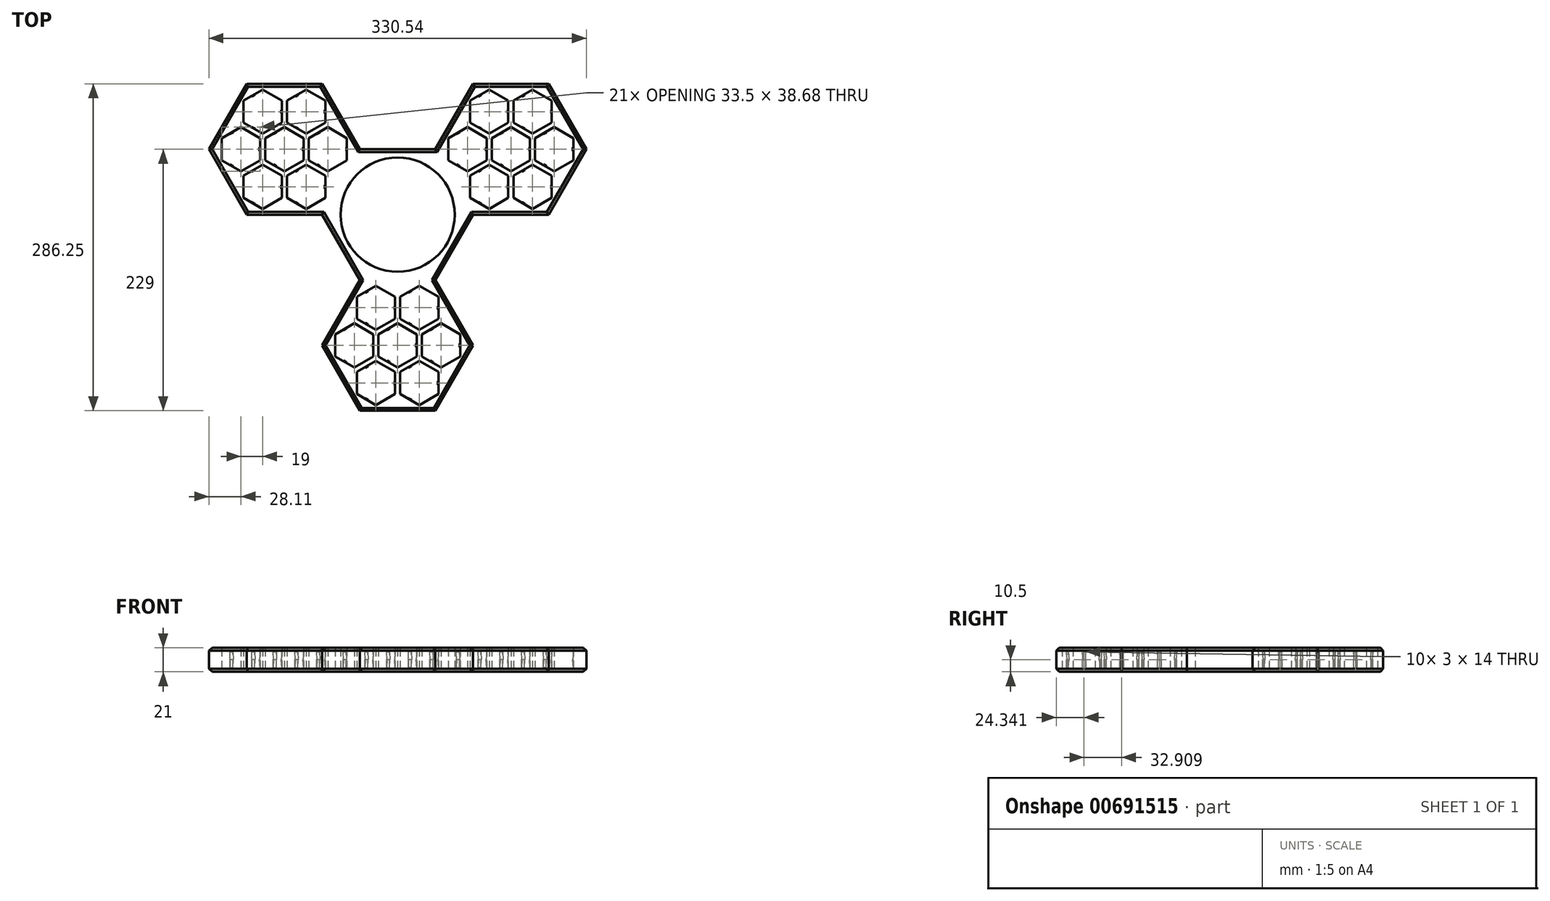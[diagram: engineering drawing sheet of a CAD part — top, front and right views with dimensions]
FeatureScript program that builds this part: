
annotation { "Feature Type Name" : "Feature", "Feature Type Description" : "" }
export const myFeature = defineFeature(function(context is Context, id is Id, definition is map)
    precondition{}
    {
        {
            var Q0;
            Q0=qCreatedBy(makeId("Top.planeOp"),FACE);
            var sketch = newSketch(context, id + "F0", { "sketchPlane" : qUnion([Q0])});
            skCircle(sketch, "E0", {"center": v(0, 0) * mm, "radius": 50 * mm});
            skCircle(sketch, "E1.cCircle", {"center": v(0, 0) * mm, "radius": 57.25 * mm, "construction": true});
            skLineSegment(sketch, "E1.0", {"start": v(-33.05, 57.25) * mm, "end": v(33.05, 57.25) * mm});
            skLineSegment(sketch, "E1.2", {"start": v(66.1, 0) * mm, "end": v(33.05, -57.25) * mm});
            skLineSegment(sketch, "E1.4", {"start": v(-33.05, -57.25) * mm, "end": v(-66.1, 0) * mm});
            skPoint(sketch, "E1.0.midPoint", {"position": v(0, 57.25) * mm});
            skCircle(sketch, "E2.cCircle", {"center": v(-61.16, 57.25) * mm, "radius": 16.75 * mm, "construction": true});
            skLineSegment(sketch, "E2.0", {"start": v(-44.4, 66.92) * mm, "end": v(-44.4, 47.58) * mm});
            skLineSegment(sketch, "E2.1", {"start": v(-44.4, 47.58) * mm, "end": v(-61.16, 37.9) * mm});
            skLineSegment(sketch, "E2.2", {"start": v(-61.16, 37.9) * mm, "end": v(-77.9, 47.58) * mm});
            skLineSegment(sketch, "E2.3", {"start": v(-77.9, 47.58) * mm, "end": v(-77.9, 66.92) * mm});
            skLineSegment(sketch, "E2.4", {"start": v(-77.9, 66.92) * mm, "end": v(-61.16, 76.6) * mm});
            skLineSegment(sketch, "E2.5", {"start": v(-61.16, 76.6) * mm, "end": v(-44.4, 66.92) * mm});
            skPoint(sketch, "E2.0.midPoint", {"position": v(-44.4, 57.25) * mm});
            skCircle(sketch, "E3.cCircle", {"center": v(-80.16, 24.34) * mm, "radius": 16.75 * mm, "construction": true});
            skLineSegment(sketch, "E3.0", {"start": v(-63.4, 34.01) * mm, "end": v(-63.4, 14.67) * mm});
            skLineSegment(sketch, "E3.1", {"start": v(-63.4, 14.67) * mm, "end": v(-80.16, 5) * mm});
            skLineSegment(sketch, "E3.2", {"start": v(-80.16, 5) * mm, "end": v(-96.9, 14.67) * mm});
            skLineSegment(sketch, "E3.3", {"start": v(-96.9, 14.67) * mm, "end": v(-96.9, 34.01) * mm});
            skLineSegment(sketch, "E3.4", {"start": v(-96.9, 34.01) * mm, "end": v(-80.16, 43.68) * mm});
            skLineSegment(sketch, "E3.5", {"start": v(-80.16, 43.68) * mm, "end": v(-63.4, 34.01) * mm});
            skPoint(sketch, "E3.0.midPoint", {"position": v(-63.4, 24.34) * mm});
            skCircle(sketch, "E4.cCircle", {"center": v(-99.16, 57.25) * mm, "radius": 16.75 * mm, "construction": true});
            skLineSegment(sketch, "E4.0", {"start": v(-82.4, 66.92) * mm, "end": v(-82.4, 47.58) * mm});
            skLineSegment(sketch, "E4.1", {"start": v(-82.4, 47.58) * mm, "end": v(-99.16, 37.9) * mm});
            skLineSegment(sketch, "E4.2", {"start": v(-99.16, 37.9) * mm, "end": v(-115.9, 47.58) * mm});
            skLineSegment(sketch, "E4.3", {"start": v(-115.9, 47.58) * mm, "end": v(-115.9, 66.92) * mm});
            skLineSegment(sketch, "E4.4", {"start": v(-115.9, 66.92) * mm, "end": v(-99.16, 76.6) * mm});
            skLineSegment(sketch, "E4.5", {"start": v(-99.16, 76.6) * mm, "end": v(-82.4, 66.92) * mm});
            skPoint(sketch, "E4.0.midPoint", {"position": v(-82.4, 57.25) * mm});
            skCircle(sketch, "E5.cCircle", {"center": v(-118.16, 24.34) * mm, "radius": 16.75 * mm, "construction": true});
            skLineSegment(sketch, "E5.0", {"start": v(-101.4, 34.01) * mm, "end": v(-101.4, 14.67) * mm});
            skLineSegment(sketch, "E5.1", {"start": v(-101.4, 14.67) * mm, "end": v(-118.16, 5) * mm});
            skLineSegment(sketch, "E5.2", {"start": v(-118.16, 5) * mm, "end": v(-134.9, 14.67) * mm});
            skLineSegment(sketch, "E5.3", {"start": v(-134.9, 14.67) * mm, "end": v(-134.9, 34.01) * mm});
            skLineSegment(sketch, "E5.4", {"start": v(-134.9, 34.01) * mm, "end": v(-118.16, 43.68) * mm});
            skLineSegment(sketch, "E5.5", {"start": v(-118.16, 43.68) * mm, "end": v(-101.4, 34.01) * mm});
            skPoint(sketch, "E5.0.midPoint", {"position": v(-101.4, 24.34) * mm});
            skCircle(sketch, "E6.cCircle", {"center": v(-80.16, 90.16) * mm, "radius": 16.75 * mm, "construction": true});
            skLineSegment(sketch, "E6.0", {"start": v(-63.4, 99.83) * mm, "end": v(-63.4, 80.49) * mm});
            skLineSegment(sketch, "E6.1", {"start": v(-63.4, 80.49) * mm, "end": v(-80.16, 70.82) * mm});
            skLineSegment(sketch, "E6.2", {"start": v(-80.16, 70.82) * mm, "end": v(-96.9, 80.49) * mm});
            skLineSegment(sketch, "E6.3", {"start": v(-96.9, 80.49) * mm, "end": v(-96.9, 99.83) * mm});
            skLineSegment(sketch, "E6.4", {"start": v(-96.9, 99.83) * mm, "end": v(-80.16, 109.5) * mm});
            skLineSegment(sketch, "E6.5", {"start": v(-80.16, 109.5) * mm, "end": v(-63.4, 99.83) * mm});
            skPoint(sketch, "E6.0.midPoint", {"position": v(-63.4, 90.16) * mm});
            skCircle(sketch, "E7.cCircle", {"center": v(-137.16, 57.25) * mm, "radius": 16.75 * mm, "construction": true});
            skLineSegment(sketch, "E7.0", {"start": v(-120.4, 66.92) * mm, "end": v(-120.4, 47.58) * mm});
            skLineSegment(sketch, "E7.1", {"start": v(-120.4, 47.58) * mm, "end": v(-137.16, 37.9) * mm});
            skLineSegment(sketch, "E7.2", {"start": v(-137.16, 37.9) * mm, "end": v(-153.9, 47.58) * mm});
            skLineSegment(sketch, "E7.3", {"start": v(-153.9, 47.58) * mm, "end": v(-153.9, 66.92) * mm});
            skLineSegment(sketch, "E7.4", {"start": v(-153.9, 66.92) * mm, "end": v(-137.16, 76.6) * mm});
            skLineSegment(sketch, "E7.5", {"start": v(-137.16, 76.6) * mm, "end": v(-120.4, 66.92) * mm});
            skPoint(sketch, "E7.0.midPoint", {"position": v(-120.4, 57.25) * mm});
            skCircle(sketch, "E8.cCircle", {"center": v(-118.16, 90.16) * mm, "radius": 16.75 * mm, "construction": true});
            skLineSegment(sketch, "E8.0", {"start": v(-101.4, 99.83) * mm, "end": v(-101.4, 80.49) * mm});
            skLineSegment(sketch, "E8.1", {"start": v(-101.4, 80.49) * mm, "end": v(-118.16, 70.82) * mm});
            skLineSegment(sketch, "E8.2", {"start": v(-118.16, 70.82) * mm, "end": v(-134.9, 80.49) * mm});
            skLineSegment(sketch, "E8.3", {"start": v(-134.9, 80.49) * mm, "end": v(-134.9, 99.83) * mm});
            skLineSegment(sketch, "E8.4", {"start": v(-134.9, 99.83) * mm, "end": v(-118.16, 109.5) * mm});
            skLineSegment(sketch, "E8.5", {"start": v(-118.16, 109.5) * mm, "end": v(-101.4, 99.83) * mm});
            skPoint(sketch, "E8.0.midPoint", {"position": v(-101.4, 90.16) * mm});
            skCircle(sketch, "E9.cCircle", {"center": v(-99.16, 57.25) * mm, "radius": 57.25 * mm, "construction": true});
            skLineSegment(sketch, "E9.0", {"start": v(-66.1, 114.5) * mm, "end": v(-33.05, 57.25) * mm});
            skLineSegment(sketch, "E9.2", {"start": v(-66.1, 0) * mm, "end": v(-132.21, 0) * mm});
            skLineSegment(sketch, "E9.3", {"start": v(-132.21, 0) * mm, "end": v(-165.27, 57.25) * mm});
            skLineSegment(sketch, "E9.4", {"start": v(-165.27, 57.25) * mm, "end": v(-132.21, 114.5) * mm});
            skLineSegment(sketch, "E9.5", {"start": v(-132.21, 114.5) * mm, "end": v(-66.1, 114.5) * mm});
            skPoint(sketch, "E9.0.midPoint", {"position": v(-49.58, 85.87) * mm});
            skLineSegment(sketch, "E10.1.0", {"start": v(19, -128.07) * mm, "end": v(35.75, -137.74) * mm});
            skLineSegment(sketch, "E10.1.1", {"start": v(-38, -95.16) * mm, "end": v(-21.25, -104.83) * mm});
            skLineSegment(sketch, "E10.1.2", {"start": v(38, -95.16) * mm, "end": v(54.75, -104.83) * mm});
            skLineSegment(sketch, "E10.1.3", {"start": v(38, -133.84) * mm, "end": v(21.25, -124.17) * mm});
            skCircle(sketch, "E10.1.4", {"center": v(38, -114.5) * mm, "radius": 16.75 * mm, "construction": true});
            skCircle(sketch, "E10.1.5", {"center": v(19, -147.4) * mm, "radius": 16.75 * mm, "construction": true});
            skLineSegment(sketch, "E10.1.6", {"start": v(-19, -62.25) * mm, "end": v(-2.25, -71.92) * mm});
            skCircle(sketch, "E10.1.7", {"center": v(-38, -114.5) * mm, "radius": 16.75 * mm, "construction": true});
            skPoint(sketch, "E10.1.8", {"position": v(-27.37, -67.09) * mm});
            skLineSegment(sketch, "E10.1.9", {"start": v(-2.25, -71.92) * mm, "end": v(-2.25, -91.26) * mm});
            skPoint(sketch, "E10.1.10", {"position": v(-8.38, -100) * mm});
            skCircle(sketch, "E10.1.12", {"center": v(-19, -81.6) * mm, "radius": 16.75 * mm, "construction": true});
            skLineSegment(sketch, "E10.1.13", {"start": v(66.1, -114.5) * mm, "end": v(33.05, -171.75) * mm});
            skPoint(sketch, "E10.1.14", {"position": v(-49.58, -85.87) * mm});
            skLineSegment(sketch, "E10.1.15", {"start": v(19, -166.75) * mm, "end": v(2.25, -157.08) * mm});
            skLineSegment(sketch, "E10.1.16", {"start": v(33.05, -57.25) * mm, "end": v(66.1, -114.5) * mm});
            skLineSegment(sketch, "E10.1.17", {"start": v(2.25, -91.26) * mm, "end": v(2.25, -71.92) * mm});
            skLineSegment(sketch, "E10.1.18", {"start": v(33.05, -171.75) * mm, "end": v(-33.05, -171.75) * mm});
            skLineSegment(sketch, "E10.1.19", {"start": v(35.75, -137.74) * mm, "end": v(35.75, -157.08) * mm});
            skLineSegment(sketch, "E10.1.20", {"start": v(-2.25, -137.74) * mm, "end": v(-2.25, -157.08) * mm});
            skPoint(sketch, "E10.1.21", {"position": v(-27.38, -132.9) * mm});
            skLineSegment(sketch, "E10.1.22", {"start": v(54.75, -124.17) * mm, "end": v(38, -133.84) * mm});
            skPoint(sketch, "E10.1.23", {"position": v(29.62, -100) * mm});
            skPoint(sketch, "E10.1.24", {"position": v(-46.37, -100) * mm});
            skCircle(sketch, "E10.1.25", {"center": v(0, -114.5) * mm, "radius": 16.75 * mm, "construction": true});
            skLineSegment(sketch, "E10.1.26", {"start": v(-2.25, -157.08) * mm, "end": v(-19, -166.75) * mm});
            skLineSegment(sketch, "E10.1.27", {"start": v(-33.05, -171.75) * mm, "end": v(-66.1, -114.5) * mm});
            skLineSegment(sketch, "E10.1.28", {"start": v(-19, -100.93) * mm, "end": v(-35.75, -91.26) * mm});
            skPoint(sketch, "E10.1.29", {"position": v(10.63, -67.09) * mm});
            skCircle(sketch, "E10.1.30", {"center": v(0, -114.5) * mm, "radius": 57.25 * mm, "construction": true});
            skLineSegment(sketch, "E10.1.31", {"start": v(-35.75, -91.26) * mm, "end": v(-35.75, -71.92) * mm});
            skCircle(sketch, "E10.1.32", {"center": v(19, -81.6) * mm, "radius": 16.75 * mm, "construction": true});
            skLineSegment(sketch, "E10.1.33", {"start": v(-38, -133.84) * mm, "end": v(-54.75, -124.17) * mm});
            skLineSegment(sketch, "E10.1.34", {"start": v(35.75, -71.92) * mm, "end": v(35.75, -91.26) * mm});
            skCircle(sketch, "E10.1.35", {"center": v(-19, -147.4) * mm, "radius": 16.75 * mm, "construction": true});
            skPoint(sketch, "E10.1.36", {"position": v(10.62, -132.9) * mm});
            skLineSegment(sketch, "E10.1.37", {"start": v(-66.1, -114.5) * mm, "end": v(-33.05, -57.25) * mm});
            skLineSegment(sketch, "E10.1.38", {"start": v(-2.25, -91.26) * mm, "end": v(-19, -100.93) * mm});
            skLineSegment(sketch, "E10.1.39", {"start": v(-19, -128.07) * mm, "end": v(-2.25, -137.74) * mm});
            skLineSegment(sketch, "E10.1.40", {"start": v(2.25, -71.92) * mm, "end": v(19, -62.25) * mm});
            skLineSegment(sketch, "E10.1.42", {"start": v(-16.75, -104.83) * mm, "end": v(0, -95.16) * mm});
            skLineSegment(sketch, "E10.1.43", {"start": v(-19, -166.75) * mm, "end": v(-35.75, -157.08) * mm});
            skLineSegment(sketch, "E10.1.44", {"start": v(-35.75, -71.92) * mm, "end": v(-19, -62.25) * mm});
            skLineSegment(sketch, "E10.1.45", {"start": v(-21.25, -104.83) * mm, "end": v(-21.25, -124.17) * mm});
            skLineSegment(sketch, "E10.1.46", {"start": v(0, -133.84) * mm, "end": v(-16.75, -124.17) * mm});
            skLineSegment(sketch, "E10.1.47", {"start": v(19, -100.93) * mm, "end": v(2.25, -91.26) * mm});
            skLineSegment(sketch, "E10.1.48", {"start": v(54.75, -104.83) * mm, "end": v(54.75, -124.17) * mm});
            skLineSegment(sketch, "E10.1.49", {"start": v(2.25, -137.74) * mm, "end": v(19, -128.07) * mm});
            skLineSegment(sketch, "E10.1.50", {"start": v(-16.75, -124.17) * mm, "end": v(-16.75, -104.83) * mm});
            skLineSegment(sketch, "E10.1.51", {"start": v(-35.75, -157.08) * mm, "end": v(-35.75, -137.74) * mm});
            skLineSegment(sketch, "E10.1.52", {"start": v(21.25, -104.83) * mm, "end": v(38, -95.16) * mm});
            skLineSegment(sketch, "E10.1.53", {"start": v(-21.25, -124.17) * mm, "end": v(-38, -133.84) * mm});
            skLineSegment(sketch, "E10.1.54", {"start": v(0, -95.16) * mm, "end": v(16.75, -104.83) * mm});
            skLineSegment(sketch, "E10.1.55", {"start": v(-54.75, -104.83) * mm, "end": v(-38, -95.16) * mm});
            skLineSegment(sketch, "E10.1.56", {"start": v(19, -62.25) * mm, "end": v(35.75, -71.92) * mm});
            skLineSegment(sketch, "E10.1.57", {"start": v(2.25, -157.08) * mm, "end": v(2.25, -137.74) * mm});
            skLineSegment(sketch, "E10.1.58", {"start": v(35.75, -157.08) * mm, "end": v(19, -166.75) * mm});
            skLineSegment(sketch, "E10.1.59", {"start": v(16.75, -104.83) * mm, "end": v(16.75, -124.17) * mm});
            skLineSegment(sketch, "E10.1.60", {"start": v(21.25, -124.17) * mm, "end": v(21.25, -104.83) * mm});
            skLineSegment(sketch, "E10.1.61", {"start": v(-35.75, -137.74) * mm, "end": v(-19, -128.07) * mm});
            skLineSegment(sketch, "E10.1.62", {"start": v(35.75, -91.26) * mm, "end": v(19, -100.93) * mm});
            skLineSegment(sketch, "E10.1.63", {"start": v(16.75, -124.17) * mm, "end": v(0, -133.84) * mm});
            skLineSegment(sketch, "E10.1.64", {"start": v(-54.75, -124.17) * mm, "end": v(-54.75, -104.83) * mm});
            skLineSegment(sketch, "E10.2.0", {"start": v(101.4, 80.49) * mm, "end": v(101.4, 99.83) * mm});
            skLineSegment(sketch, "E10.2.1", {"start": v(101.4, 14.67) * mm, "end": v(101.4, 34.01) * mm});
            skLineSegment(sketch, "E10.2.2", {"start": v(63.4, 80.49) * mm, "end": v(63.4, 99.83) * mm});
            skLineSegment(sketch, "E10.2.3", {"start": v(96.9, 99.83) * mm, "end": v(96.9, 80.49) * mm});
            skCircle(sketch, "E10.2.4", {"center": v(80.16, 90.16) * mm, "radius": 16.75 * mm, "construction": true});
            skCircle(sketch, "E10.2.5", {"center": v(118.16, 90.16) * mm, "radius": 16.75 * mm, "construction": true});
            skLineSegment(sketch, "E10.2.6", {"start": v(63.4, 14.67) * mm, "end": v(63.4, 34.01) * mm});
            skCircle(sketch, "E10.2.7", {"center": v(118.16, 24.34) * mm, "radius": 16.75 * mm, "construction": true});
            skPoint(sketch, "E10.2.8", {"position": v(71.78, 9.84) * mm});
            skLineSegment(sketch, "E10.2.9", {"start": v(63.4, 34.01) * mm, "end": v(80.16, 43.68) * mm});
            skPoint(sketch, "E10.2.10", {"position": v(90.78, 42.74) * mm});
            skCircle(sketch, "E10.2.12", {"center": v(80.16, 24.34) * mm, "radius": 16.75 * mm, "construction": true});
            skLineSegment(sketch, "E10.2.13", {"start": v(66.1, 114.5) * mm, "end": v(132.21, 114.5) * mm});
            skPoint(sketch, "E10.2.14", {"position": v(99.16, 0) * mm});
            skLineSegment(sketch, "E10.2.15", {"start": v(134.9, 99.83) * mm, "end": v(134.9, 80.49) * mm});
            skLineSegment(sketch, "E10.2.16", {"start": v(33.05, 57.25) * mm, "end": v(66.1, 114.5) * mm});
            skLineSegment(sketch, "E10.2.17", {"start": v(77.9, 47.58) * mm, "end": v(61.16, 37.9) * mm});
            skLineSegment(sketch, "E10.2.18", {"start": v(132.21, 114.5) * mm, "end": v(165.27, 57.25) * mm});
            skLineSegment(sketch, "E10.2.19", {"start": v(101.4, 99.83) * mm, "end": v(118.16, 109.5) * mm});
            skLineSegment(sketch, "E10.2.20", {"start": v(120.4, 66.92) * mm, "end": v(137.16, 76.6) * mm});
            skPoint(sketch, "E10.2.21", {"position": v(128.78, 42.74) * mm});
            skLineSegment(sketch, "E10.2.22", {"start": v(80.16, 109.5) * mm, "end": v(96.9, 99.83) * mm});
            skPoint(sketch, "E10.2.23", {"position": v(71.78, 75.65) * mm});
            skPoint(sketch, "E10.2.24", {"position": v(109.78, 9.84) * mm});
            skCircle(sketch, "E10.2.25", {"center": v(99.16, 57.25) * mm, "radius": 16.75 * mm, "construction": true});
            skLineSegment(sketch, "E10.2.26", {"start": v(137.16, 76.6) * mm, "end": v(153.9, 66.92) * mm});
            skLineSegment(sketch, "E10.2.27", {"start": v(165.27, 57.25) * mm, "end": v(132.21, 0) * mm});
            skLineSegment(sketch, "E10.2.28", {"start": v(96.9, 34.01) * mm, "end": v(96.9, 14.67) * mm});
            skPoint(sketch, "E10.2.29", {"position": v(52.78, 42.74) * mm});
            skCircle(sketch, "E10.2.30", {"center": v(99.16, 57.25) * mm, "radius": 57.25 * mm, "construction": true});
            skLineSegment(sketch, "E10.2.31", {"start": v(96.9, 14.67) * mm, "end": v(80.16, 5) * mm});
            skCircle(sketch, "E10.2.32", {"center": v(61.16, 57.25) * mm, "radius": 16.75 * mm, "construction": true});
            skLineSegment(sketch, "E10.2.33", {"start": v(134.9, 34.01) * mm, "end": v(134.9, 14.67) * mm});
            skLineSegment(sketch, "E10.2.34", {"start": v(44.4, 66.92) * mm, "end": v(61.16, 76.6) * mm});
            skCircle(sketch, "E10.2.35", {"center": v(137.16, 57.25) * mm, "radius": 16.75 * mm, "construction": true});
            skPoint(sketch, "E10.2.36", {"position": v(109.78, 75.65) * mm});
            skLineSegment(sketch, "E10.2.37", {"start": v(132.21, 0) * mm, "end": v(66.1, 0) * mm});
            skLineSegment(sketch, "E10.2.38", {"start": v(80.16, 43.68) * mm, "end": v(96.9, 34.01) * mm});
            skLineSegment(sketch, "E10.2.39", {"start": v(120.4, 47.58) * mm, "end": v(120.4, 66.92) * mm});
            skLineSegment(sketch, "E10.2.40", {"start": v(61.16, 37.9) * mm, "end": v(44.4, 47.58) * mm});
            skLineSegment(sketch, "E10.2.42", {"start": v(99.16, 37.9) * mm, "end": v(82.4, 47.58) * mm});
            skLineSegment(sketch, "E10.2.43", {"start": v(153.9, 66.92) * mm, "end": v(153.9, 47.58) * mm});
            skLineSegment(sketch, "E10.2.44", {"start": v(80.16, 5) * mm, "end": v(63.4, 14.67) * mm});
            skLineSegment(sketch, "E10.2.45", {"start": v(101.4, 34.01) * mm, "end": v(118.16, 43.68) * mm});
            skLineSegment(sketch, "E10.2.46", {"start": v(115.9, 66.92) * mm, "end": v(115.9, 47.58) * mm});
            skLineSegment(sketch, "E10.2.47", {"start": v(77.9, 66.92) * mm, "end": v(77.9, 47.58) * mm});
            skLineSegment(sketch, "E10.2.48", {"start": v(63.4, 99.83) * mm, "end": v(80.16, 109.5) * mm});
            skLineSegment(sketch, "E10.2.49", {"start": v(118.16, 70.82) * mm, "end": v(101.4, 80.49) * mm});
            skLineSegment(sketch, "E10.2.50", {"start": v(115.9, 47.58) * mm, "end": v(99.16, 37.9) * mm});
            skLineSegment(sketch, "E10.2.51", {"start": v(153.9, 47.58) * mm, "end": v(137.16, 37.9) * mm});
            skLineSegment(sketch, "E10.2.52", {"start": v(80.16, 70.82) * mm, "end": v(63.4, 80.49) * mm});
            skLineSegment(sketch, "E10.2.53", {"start": v(118.16, 43.68) * mm, "end": v(134.9, 34.01) * mm});
            skLineSegment(sketch, "E10.2.54", {"start": v(82.4, 47.58) * mm, "end": v(82.4, 66.92) * mm});
            skLineSegment(sketch, "E10.2.55", {"start": v(118.16, 5) * mm, "end": v(101.4, 14.67) * mm});
            skLineSegment(sketch, "E10.2.56", {"start": v(44.4, 47.58) * mm, "end": v(44.4, 66.92) * mm});
            skLineSegment(sketch, "E10.2.57", {"start": v(134.9, 80.49) * mm, "end": v(118.16, 70.82) * mm});
            skLineSegment(sketch, "E10.2.58", {"start": v(118.16, 109.5) * mm, "end": v(134.9, 99.83) * mm});
            skLineSegment(sketch, "E10.2.59", {"start": v(82.4, 66.92) * mm, "end": v(99.16, 76.6) * mm});
            skLineSegment(sketch, "E10.2.60", {"start": v(96.9, 80.49) * mm, "end": v(80.16, 70.82) * mm});
            skLineSegment(sketch, "E10.2.61", {"start": v(137.16, 37.9) * mm, "end": v(120.4, 47.58) * mm});
            skLineSegment(sketch, "E10.2.62", {"start": v(61.16, 76.6) * mm, "end": v(77.9, 66.92) * mm});
            skLineSegment(sketch, "E10.2.63", {"start": v(99.16, 76.6) * mm, "end": v(115.9, 66.92) * mm});
            skLineSegment(sketch, "E10.2.64", {"start": v(134.9, 14.67) * mm, "end": v(118.16, 5) * mm});
            skSolve(sketch);
        }
        {
            var Q0;
            Q0=makeQuery(id+"F0.imprint","IMPRINT",FACE,{"disambiguationData":[TD([[makeQuery(id+"F0.imprint","IMPRINT",EDGE,{"derivedFrom":sQuery(id+"F0.wireOp",EDGE,"E0")}),-1.0]])]});
            extrude(context, id + "F1", {"entities" : qUnion([Q0]), "depth" : 21 * mm, "offsetDistance" : 25 * mm});
        }
        {
            var Q0;
            Q0=makeQuery(id+"F1.opExtrude","CAP_EDGE",EDGE,{"disambiguationData":[OSD([sQuery(id+"F0.wireOp",EDGE,"E1.2")])],"isStart":false});
            var Q1;
            Q1=makeQuery(id+"F1.opExtrude","CAP_EDGE",EDGE,{"disambiguationData":[OSD([sQuery(id+"F0.wireOp",EDGE,"E10.2.37")])],"isStart":false});
            var Q2;
            Q2=makeQuery(id+"F1.opExtrude","CAP_EDGE",EDGE,{"disambiguationData":[OSD([sQuery(id+"F0.wireOp",EDGE,"E10.1.16")])],"isStart":false});
            var Q3;
            Q3=makeQuery(id+"F1.opExtrude","CAP_EDGE",EDGE,{"disambiguationData":[OSD([sQuery(id+"F0.wireOp",EDGE,"E10.1.13")])],"isStart":false});
            var Q4;
            Q4=makeQuery(id+"F1.opExtrude","CAP_EDGE",EDGE,{"disambiguationData":[OSD([sQuery(id+"F0.wireOp",EDGE,"E10.1.18")])],"isStart":false});
            var Q5;
            Q5=makeQuery(id+"F1.opExtrude","CAP_EDGE",EDGE,{"disambiguationData":[OSD([sQuery(id+"F0.wireOp",EDGE,"E10.1.27")])],"isStart":false});
            var Q6;
            Q6=makeQuery(id+"F1.opExtrude","CAP_EDGE",EDGE,{"disambiguationData":[OSD([sQuery(id+"F0.wireOp",EDGE,"E10.1.37")])],"isStart":false});
            var Q7;
            Q7=makeQuery(id+"F1.opExtrude","CAP_EDGE",EDGE,{"disambiguationData":[OSD([sQuery(id+"F0.wireOp",EDGE,"E1.4")])],"isStart":false});
            var Q8;
            Q8=makeQuery(id+"F1.opExtrude","CAP_EDGE",EDGE,{"disambiguationData":[OSD([sQuery(id+"F0.wireOp",EDGE,"E9.2")])],"isStart":false});
            var Q9;
            Q9=makeQuery(id+"F1.opExtrude","CAP_EDGE",EDGE,{"disambiguationData":[OSD([sQuery(id+"F0.wireOp",EDGE,"E9.3")])],"isStart":false});
            var Q10;
            Q10=makeQuery(id+"F1.opExtrude","CAP_EDGE",EDGE,{"disambiguationData":[OSD([sQuery(id+"F0.wireOp",EDGE,"E9.4")])],"isStart":false});
            var Q11;
            Q11=makeQuery(id+"F1.opExtrude","CAP_EDGE",EDGE,{"disambiguationData":[OSD([sQuery(id+"F0.wireOp",EDGE,"E9.5")])],"isStart":false});
            var Q12;
            Q12=makeQuery(id+"F1.opExtrude","CAP_EDGE",EDGE,{"disambiguationData":[OSD([sQuery(id+"F0.wireOp",EDGE,"E9.0")])],"isStart":false});
            var Q13;
            Q13=makeQuery(id+"F1.opExtrude","CAP_EDGE",EDGE,{"disambiguationData":[OSD([sQuery(id+"F0.wireOp",EDGE,"E1.0")])],"isStart":false});
            var Q14;
            Q14=makeQuery(id+"F1.opExtrude","CAP_EDGE",EDGE,{"disambiguationData":[OSD([sQuery(id+"F0.wireOp",EDGE,"E10.2.16")])],"isStart":false});
            var Q15;
            Q15=makeQuery(id+"F1.opExtrude","CAP_EDGE",EDGE,{"disambiguationData":[OSD([sQuery(id+"F0.wireOp",EDGE,"E10.2.27")])],"isStart":false});
            var Q16;
            Q16=makeQuery(id+"F1.opExtrude","CAP_EDGE",EDGE,{"disambiguationData":[OSD([sQuery(id+"F0.wireOp",EDGE,"E10.2.18")])],"isStart":false});
            var Q17;
            Q17=makeQuery(id+"F1.opExtrude","CAP_EDGE",EDGE,{"disambiguationData":[OSD([sQuery(id+"F0.wireOp",EDGE,"E10.2.13")])],"isStart":false});
            var Q18;
            Q18=makeQuery(id+"F1.opExtrude","CAP_EDGE",EDGE,{"disambiguationData":[OSD([sQuery(id+"F0.wireOp",EDGE,"E10.1.13")])],"isStart":true});
            var Q19;
            Q19=makeQuery(id+"F1.opExtrude","CAP_EDGE",EDGE,{"disambiguationData":[OSD([sQuery(id+"F0.wireOp",EDGE,"E10.1.18")])],"isStart":true});
            var Q20;
            Q20=makeQuery(id+"F1.opExtrude","CAP_EDGE",EDGE,{"disambiguationData":[OSD([sQuery(id+"F0.wireOp",EDGE,"E10.1.27")])],"isStart":true});
            var Q21;
            Q21=makeQuery(id+"F1.opExtrude","CAP_EDGE",EDGE,{"disambiguationData":[OSD([sQuery(id+"F0.wireOp",EDGE,"E10.1.37")])],"isStart":true});
            var Q22;
            Q22=makeQuery(id+"F1.opExtrude","CAP_EDGE",EDGE,{"disambiguationData":[OSD([sQuery(id+"F0.wireOp",EDGE,"E1.4")])],"isStart":true});
            var Q23;
            Q23=makeQuery(id+"F1.opExtrude","CAP_EDGE",EDGE,{"disambiguationData":[OSD([sQuery(id+"F0.wireOp",EDGE,"E9.2")])],"isStart":true});
            var Q24;
            Q24=makeQuery(id+"F1.opExtrude","CAP_EDGE",EDGE,{"disambiguationData":[OSD([sQuery(id+"F0.wireOp",EDGE,"E9.3")])],"isStart":true});
            var Q25;
            Q25=makeQuery(id+"F1.opExtrude","CAP_EDGE",EDGE,{"disambiguationData":[OSD([sQuery(id+"F0.wireOp",EDGE,"E10.1.16")])],"isStart":true});
            var Q26;
            Q26=makeQuery(id+"F1.opExtrude","CAP_EDGE",EDGE,{"disambiguationData":[OSD([sQuery(id+"F0.wireOp",EDGE,"E1.2")])],"isStart":true});
            var Q27;
            Q27=makeQuery(id+"F1.opExtrude","CAP_EDGE",EDGE,{"disambiguationData":[OSD([sQuery(id+"F0.wireOp",EDGE,"E10.2.37")])],"isStart":true});
            var Q28;
            Q28=makeQuery(id+"F1.opExtrude","CAP_EDGE",EDGE,{"disambiguationData":[OSD([sQuery(id+"F0.wireOp",EDGE,"E10.2.27")])],"isStart":true});
            var Q29;
            Q29=makeQuery(id+"F1.opExtrude","CAP_EDGE",EDGE,{"disambiguationData":[OSD([sQuery(id+"F0.wireOp",EDGE,"E10.2.18")])],"isStart":true});
            var Q30;
            Q30=makeQuery(id+"F1.opExtrude","CAP_EDGE",EDGE,{"disambiguationData":[OSD([sQuery(id+"F0.wireOp",EDGE,"E10.2.13")])],"isStart":true});
            var Q31;
            Q31=makeQuery(id+"F1.opExtrude","CAP_EDGE",EDGE,{"disambiguationData":[OSD([sQuery(id+"F0.wireOp",EDGE,"E10.2.16")])],"isStart":true});
            var Q32;
            Q32=makeQuery(id+"F1.opExtrude","CAP_EDGE",EDGE,{"disambiguationData":[OSD([sQuery(id+"F0.wireOp",EDGE,"E1.0")])],"isStart":true});
            var Q33;
            Q33=makeQuery(id+"F1.opExtrude","CAP_EDGE",EDGE,{"disambiguationData":[OSD([sQuery(id+"F0.wireOp",EDGE,"E9.0")])],"isStart":true});
            var Q34;
            Q34=makeQuery(id+"F1.opExtrude","CAP_EDGE",EDGE,{"disambiguationData":[OSD([sQuery(id+"F0.wireOp",EDGE,"E9.5")])],"isStart":true});
            var Q35;
            Q35=makeQuery(id+"F1.opExtrude","CAP_EDGE",EDGE,{"disambiguationData":[OSD([sQuery(id+"F0.wireOp",EDGE,"E9.4")])],"isStart":true});
            chamfer(context, id + "F2", {"entities" : qUnion([Q0, Q1, Q2, Q3, Q4, Q5, Q6, Q7, Q8, Q9, Q10, Q11, Q12, Q13, Q14, Q15, Q16, Q17, Q18, Q19, Q20, Q21, Q22, Q23, Q24, Q25, Q26, Q27, Q28, Q29, Q30, Q31, Q32, Q33, Q34, Q35]), "width" : 2.5 * mm, "tangentPropagation" : true});
        }
        {
            var Q0;
            Q0=makeQuery(id+"F1.opExtrude","SWEPT_FACE",FACE,{"disambiguationData":[OSD([sQuery(id+"F0.wireOp",EDGE,"E8.4")])]});
            var sketch = newSketch(context, id + "F3", { "sketchPlane" : qUnion([Q0])});
            skLineSegment(sketch, "E11.bottom", {"start": v(-55.75, 3.5) * mm, "end": v(-58.75, 3.5) * mm});
            skLineSegment(sketch, "E11.top", {"start": v(-55.75, 17.5) * mm, "end": v(-58.75, 17.5) * mm});
            skLineSegment(sketch, "E11.left", {"start": v(-55.75, 3.5) * mm, "end": v(-55.75, 17.5) * mm});
            skLineSegment(sketch, "E11.right", {"start": v(-58.75, 3.5) * mm, "end": v(-58.75, 17.5) * mm});
            skPoint(sketch, "E11.middle", {"position": v(-57.25, 10.5) * mm});
            skSolve(sketch);
        }
        {
            var Q0;
            Q0=makeQuery(id+"F3.imprint","IMPRINT",FACE,{"disambiguationData":[TD([[makeQuery(id+"F3.imprint","IMPRINT",EDGE,{"derivedFrom":sQuery(id+"F3.wireOp",EDGE,"E11.bottom")}),-1.0]])]});
            extrude(context, id + "F4", {"entities" : qUnion([Q0]), "operationType" : NewBodyOperationType.ADD, "depth" : .5 * mm, "offsetDistance" : 25 * mm});
        }
        {
            var Q0;
            Q0=makeQuery(id+"F4.opExtrude","CAP_EDGE",EDGE,{"disambiguationData":[OSD([sQuery(id+"F3.wireOp",EDGE,"E11.top")])],"isStart":false});
            var Q1;
            Q1=makeQuery(id+"F4.opExtrude","CAP_EDGE",EDGE,{"disambiguationData":[OSD([sQuery(id+"F3.wireOp",EDGE,"E11.bottom")])],"isStart":false});
            chamfer(context, id + "F5", {"entities" : qUnion([Q0, Q1]), "chamferType" : ChamferType.TWO_OFFSETS, "width1" : 7 * mm, "oppositeDirection" : false, "width2" : .5 * mm, "tangentPropagation" : true});
        }
        {
            var Q0;
            Q0=makeQuery(id+"F1.opExtrude","SWEPT_FACE",FACE,{"disambiguationData":[OSD([sQuery(id+"F0.wireOp",EDGE,"E6.4")])]});
            var sketch = newSketch(context, id + "F6", { "sketchPlane" : qUnion([Q0])});
            skLineSegment(sketch, "E12.bottom", {"start": v(-22.84, 3.5) * mm, "end": v(-25.84, 3.5) * mm});
            skLineSegment(sketch, "E12.top", {"start": v(-22.84, 17.5) * mm, "end": v(-25.84, 17.5) * mm});
            skLineSegment(sketch, "E12.left", {"start": v(-22.84, 3.5) * mm, "end": v(-22.84, 17.5) * mm});
            skLineSegment(sketch, "E12.right", {"start": v(-25.84, 3.5) * mm, "end": v(-25.84, 17.5) * mm});
            skPoint(sketch, "E12.middle", {"position": v(-24.34, 10.5) * mm});
            skLineSegment(sketch, "E13.bottom", {"start": v(-88.66, 3.5) * mm, "end": v(-91.66, 3.5) * mm});
            skLineSegment(sketch, "E13.top", {"start": v(-88.66, 17.5) * mm, "end": v(-91.66, 17.5) * mm});
            skLineSegment(sketch, "E13.left", {"start": v(-88.66, 3.5) * mm, "end": v(-88.66, 17.5) * mm});
            skLineSegment(sketch, "E13.right", {"start": v(-91.66, 3.5) * mm, "end": v(-91.66, 17.5) * mm});
            skPoint(sketch, "E13.middle", {"position": v(-90.16, 10.5) * mm});
            skSolve(sketch);
        }
        {
            var Q0;
            Q0=makeQuery(id+"F6.imprint","IMPRINT",FACE,{"disambiguationData":[TD([[makeQuery(id+"F6.imprint","IMPRINT",EDGE,{"derivedFrom":sQuery(id+"F6.wireOp",EDGE,"E13.bottom")}),-1.0]])]});
            var Q1;
            Q1=makeQuery(id+"F6.imprint","IMPRINT",FACE,{"disambiguationData":[TD([[makeQuery(id+"F6.imprint","IMPRINT",EDGE,{"derivedFrom":sQuery(id+"F6.wireOp",EDGE,"E12.bottom")}),-1.0]])]});
            extrude(context, id + "F7", {"entities" : qUnion([Q0, Q1]), "operationType" : NewBodyOperationType.ADD, "depth" : .5 * mm, "offsetDistance" : 25 * mm});
        }
        {
            var Q0;
            Q0=makeQuery(id+"F7.opExtrude","CAP_EDGE",EDGE,{"disambiguationData":[OSD([sQuery(id+"F6.wireOp",EDGE,"E13.top")])],"isStart":false});
            var Q1;
            Q1=makeQuery(id+"F7.opExtrude","CAP_EDGE",EDGE,{"disambiguationData":[OSD([sQuery(id+"F6.wireOp",EDGE,"E13.bottom")])],"isStart":false});
            var Q2;
            Q2=makeQuery(id+"F7.opExtrude","CAP_EDGE",EDGE,{"disambiguationData":[OSD([sQuery(id+"F6.wireOp",EDGE,"E12.top")])],"isStart":false});
            chamfer(context, id + "F8", {"entities" : qUnion([Q0, Q1, Q2]), "chamferType" : ChamferType.TWO_OFFSETS, "width1" : 7 * mm, "oppositeDirection" : false, "width2" : .5 * mm, "tangentPropagation" : true});
        }
        {
            var Q0;
            Q0=makeQuery(id+"F7.opExtrude","CAP_EDGE",EDGE,{"disambiguationData":[OSD([sQuery(id+"F6.wireOp",EDGE,"E12.bottom")])],"isStart":false});
            chamfer(context, id + "F9", {"entities" : qUnion([Q0]), "chamferType" : ChamferType.TWO_OFFSETS, "width1" : 7 * mm, "oppositeDirection" : true, "width2" : .5 * mm, "tangentPropagation" : true});
        }
        {
            var Q0;
            Q0=makeQuery(id+"F1.opExtrude","SWEPT_FACE",FACE,{"disambiguationData":[OSD([sQuery(id+"F0.wireOp",EDGE,"E4.4")])]});
            var sketch = newSketch(context, id + "F10", { "sketchPlane" : qUnion([Q0])});
            skLineSegment(sketch, "E14.bottom", {"start": v(-55.75, 3.5) * mm, "end": v(-58.75, 3.5) * mm});
            skLineSegment(sketch, "E14.top", {"start": v(-55.75, 17.5) * mm, "end": v(-58.75, 17.5) * mm});
            skLineSegment(sketch, "E14.left", {"start": v(-55.75, 3.5) * mm, "end": v(-55.75, 17.5) * mm});
            skLineSegment(sketch, "E14.right", {"start": v(-58.75, 3.5) * mm, "end": v(-58.75, 17.5) * mm});
            skPoint(sketch, "E14.middle", {"position": v(-57.25, 10.5) * mm});
            skSolve(sketch);
        }
        {
            var Q0;
            Q0=makeQuery(id+"F10.imprint","IMPRINT",FACE,{"disambiguationData":[TD([[makeQuery(id+"F10.imprint","IMPRINT",EDGE,{"derivedFrom":sQuery(id+"F10.wireOp",EDGE,"E14.bottom")}),-1.0]])]});
            extrude(context, id + "F11", {"entities" : qUnion([Q0]), "operationType" : NewBodyOperationType.ADD, "depth" : .5 * mm, "offsetDistance" : 25 * mm});
        }
        {
            var Q0;
            Q0=makeQuery(id+"F11.opExtrude","CAP_EDGE",EDGE,{"disambiguationData":[OSD([sQuery(id+"F10.wireOp",EDGE,"E14.top")])],"isStart":false});
            var Q1;
            Q1=makeQuery(id+"F11.opExtrude","CAP_EDGE",EDGE,{"disambiguationData":[OSD([sQuery(id+"F10.wireOp",EDGE,"E14.bottom")])],"isStart":false});
            chamfer(context, id + "F12", {"entities" : qUnion([Q0, Q1]), "chamferType" : ChamferType.TWO_OFFSETS, "width1" : 7 * mm, "oppositeDirection" : false, "width2" : .5 * mm, "tangentPropagation" : true});
        }
        {
            var Q0;
            Q0=makeQuery(id+"F1.opExtrude","SWEPT_FACE",FACE,{"disambiguationData":[OSD([sQuery(id+"F0.wireOp",EDGE,"E2.4")])]});
            var sketch = newSketch(context, id + "F13", { "sketchPlane" : qUnion([Q0])});
            skLineSegment(sketch, "E15.bottom", {"start": v(-22.84, 3.5) * mm, "end": v(-25.84, 3.5) * mm});
            skLineSegment(sketch, "E15.top", {"start": v(-22.84, 17.5) * mm, "end": v(-25.84, 17.5) * mm});
            skLineSegment(sketch, "E15.left", {"start": v(-22.84, 3.5) * mm, "end": v(-22.84, 17.5) * mm});
            skLineSegment(sketch, "E15.right", {"start": v(-25.84, 3.5) * mm, "end": v(-25.84, 17.5) * mm});
            skPoint(sketch, "E15.middle", {"position": v(-24.34, 10.5) * mm});
            skLineSegment(sketch, "E16.bottom", {"start": v(-88.66, 3.5) * mm, "end": v(-91.66, 3.5) * mm});
            skLineSegment(sketch, "E16.top", {"start": v(-88.66, 17.5) * mm, "end": v(-91.66, 17.5) * mm});
            skLineSegment(sketch, "E16.left", {"start": v(-88.66, 3.5) * mm, "end": v(-88.66, 17.5) * mm});
            skLineSegment(sketch, "E16.right", {"start": v(-91.66, 3.5) * mm, "end": v(-91.66, 17.5) * mm});
            skPoint(sketch, "E16.middle", {"position": v(-90.16, 10.5) * mm});
            skSolve(sketch);
        }
        {
            var Q0;
            Q0=makeQuery(id+"F13.imprint","IMPRINT",FACE,{"disambiguationData":[TD([[makeQuery(id+"F13.imprint","IMPRINT",EDGE,{"derivedFrom":sQuery(id+"F13.wireOp",EDGE,"E16.bottom")}),-1.0]])]});
            var Q1;
            Q1=makeQuery(id+"F13.imprint","IMPRINT",FACE,{"disambiguationData":[TD([[makeQuery(id+"F13.imprint","IMPRINT",EDGE,{"derivedFrom":sQuery(id+"F13.wireOp",EDGE,"E15.bottom")}),-1.0]])]});
            extrude(context, id + "F14", {"entities" : qUnion([Q0, Q1]), "operationType" : NewBodyOperationType.ADD, "depth" : .5 * mm, "offsetDistance" : 25 * mm});
        }
        {
            var Q0;
            Q0=makeQuery(id+"F14.opExtrude","CAP_EDGE",EDGE,{"disambiguationData":[OSD([sQuery(id+"F13.wireOp",EDGE,"E16.top")])],"isStart":false});
            var Q1;
            Q1=makeQuery(id+"F14.opExtrude","CAP_EDGE",EDGE,{"disambiguationData":[OSD([sQuery(id+"F13.wireOp",EDGE,"E16.bottom")])],"isStart":false});
            var Q2;
            Q2=makeQuery(id+"F14.opExtrude","CAP_EDGE",EDGE,{"disambiguationData":[OSD([sQuery(id+"F13.wireOp",EDGE,"E15.top")])],"isStart":false});
            chamfer(context, id + "F15", {"entities" : qUnion([Q0, Q1, Q2]), "chamferType" : ChamferType.TWO_OFFSETS, "width1" : 7 * mm, "oppositeDirection" : false, "width2" : .5 * mm, "tangentPropagation" : true});
        }
        {
            var Q0;
            Q0=makeQuery(id+"F14.opExtrude","CAP_EDGE",EDGE,{"disambiguationData":[OSD([sQuery(id+"F13.wireOp",EDGE,"E15.bottom")])],"isStart":false});
            chamfer(context, id + "F16", {"entities" : qUnion([Q0]), "chamferType" : ChamferType.TWO_OFFSETS, "width1" : 7 * mm, "oppositeDirection" : true, "width2" : .5 * mm, "tangentPropagation" : true});
        }
        {
            var Q0;
            Q0=makeQuery(id+"F1.opExtrude","SWEPT_FACE",FACE,{"disambiguationData":[OSD([sQuery(id+"F0.wireOp",EDGE,"E3.4")])]});
            var sketch = newSketch(context, id + "F17", { "sketchPlane" : qUnion([Q0])});
            skLineSegment(sketch, "E17.bottom", {"start": v(-55.75, 3.5) * mm, "end": v(-58.75, 3.5) * mm});
            skLineSegment(sketch, "E17.top", {"start": v(-55.75, 17.5) * mm, "end": v(-58.75, 17.5) * mm});
            skLineSegment(sketch, "E17.left", {"start": v(-55.75, 3.5) * mm, "end": v(-55.75, 17.5) * mm});
            skLineSegment(sketch, "E17.right", {"start": v(-58.75, 3.5) * mm, "end": v(-58.75, 17.5) * mm});
            skPoint(sketch, "E17.middle", {"position": v(-57.25, 10.5) * mm});
            skSolve(sketch);
        }
        {
            var Q0;
            Q0=makeQuery(id+"F17.imprint","IMPRINT",FACE,{"disambiguationData":[TD([[makeQuery(id+"F17.imprint","IMPRINT",EDGE,{"derivedFrom":sQuery(id+"F17.wireOp",EDGE,"E17.bottom")}),-1.0]])]});
            extrude(context, id + "F18", {"entities" : qUnion([Q0]), "operationType" : NewBodyOperationType.ADD, "depth" : .5 * mm, "offsetDistance" : 25 * mm});
        }
        {
            var Q0;
            Q0=makeQuery(id+"F18.opExtrude","CAP_EDGE",EDGE,{"disambiguationData":[OSD([sQuery(id+"F17.wireOp",EDGE,"E17.top")])],"isStart":false});
            var Q1;
            Q1=makeQuery(id+"F18.opExtrude","CAP_EDGE",EDGE,{"disambiguationData":[OSD([sQuery(id+"F17.wireOp",EDGE,"E17.bottom")])],"isStart":false});
            chamfer(context, id + "F19", {"entities" : qUnion([Q0, Q1]), "chamferType" : ChamferType.TWO_OFFSETS, "width1" : 7 * mm, "oppositeDirection" : false, "width2" : .5 * mm, "tangentPropagation" : true});
        }
        {
            var Q0;
            Q0=makeQuery(id+"F1.opExtrude","SWEPT_FACE",FACE,{"disambiguationData":[OSD([sQuery(id+"F0.wireOp",EDGE,"E10.2.48")])]});
            var sketch = newSketch(context, id + "F20", { "sketchPlane" : qUnion([Q0])});
            skLineSegment(sketch, "E18.bottom", {"start": v(116, 3.5) * mm, "end": v(113, 3.5) * mm});
            skLineSegment(sketch, "E18.top", {"start": v(116, 17.5) * mm, "end": v(113, 17.5) * mm});
            skLineSegment(sketch, "E18.left", {"start": v(116, 3.5) * mm, "end": v(116, 17.5) * mm});
            skLineSegment(sketch, "E18.right", {"start": v(113, 3.5) * mm, "end": v(113, 17.5) * mm});
            skPoint(sketch, "E18.middle", {"position": v(114.5, 10.5) * mm});
            skSolve(sketch);
        }
        {
            var Q0;
            Q0=makeQuery(id+"F20.imprint","IMPRINT",FACE,{"disambiguationData":[TD([[makeQuery(id+"F20.imprint","IMPRINT",EDGE,{"derivedFrom":sQuery(id+"F20.wireOp",EDGE,"E18.bottom")}),-1.0]])]});
            extrude(context, id + "F21", {"entities" : qUnion([Q0]), "operationType" : NewBodyOperationType.ADD, "depth" : .5 * mm, "offsetDistance" : 25 * mm});
        }
        {
            var Q0;
            Q0=makeQuery(id+"F21.opExtrude","CAP_EDGE",EDGE,{"disambiguationData":[OSD([sQuery(id+"F20.wireOp",EDGE,"E18.top")])],"isStart":false});
            var Q1;
            Q1=makeQuery(id+"F21.opExtrude","CAP_EDGE",EDGE,{"disambiguationData":[OSD([sQuery(id+"F20.wireOp",EDGE,"E18.bottom")])],"isStart":false});
            chamfer(context, id + "F22", {"entities" : qUnion([Q0, Q1]), "chamferType" : ChamferType.TWO_OFFSETS, "width1" : 7 * mm, "oppositeDirection" : false, "width2" : .5 * mm, "tangentPropagation" : true});
        }
        {
            var Q0;
            Q0=makeQuery(id+"F1.opExtrude","SWEPT_FACE",FACE,{"disambiguationData":[OSD([sQuery(id+"F0.wireOp",EDGE,"E10.2.19")])]});
            var sketch = newSketch(context, id + "F23", { "sketchPlane" : qUnion([Q0])});
            skLineSegment(sketch, "E19.bottom", {"start": v(148.9, 3.5) * mm, "end": v(145.9, 3.5) * mm});
            skLineSegment(sketch, "E19.top", {"start": v(148.9, 17.5) * mm, "end": v(145.9, 17.5) * mm});
            skLineSegment(sketch, "E19.left", {"start": v(148.9, 3.5) * mm, "end": v(148.9, 17.5) * mm});
            skLineSegment(sketch, "E19.right", {"start": v(145.9, 3.5) * mm, "end": v(145.9, 17.5) * mm});
            skPoint(sketch, "E19.middle", {"position": v(147.4, 10.5) * mm});
            skLineSegment(sketch, "E20.bottom", {"start": v(83.1, 3.5) * mm, "end": v(80.1, 3.5) * mm});
            skLineSegment(sketch, "E20.top", {"start": v(83.1, 17.5) * mm, "end": v(80.1, 17.5) * mm});
            skLineSegment(sketch, "E20.left", {"start": v(83.1, 3.5) * mm, "end": v(83.1, 17.5) * mm});
            skLineSegment(sketch, "E20.right", {"start": v(80.1, 3.5) * mm, "end": v(80.1, 17.5) * mm});
            skPoint(sketch, "E20.middle", {"position": v(81.6, 10.5) * mm});
            skSolve(sketch);
        }
        {
            var Q0;
            Q0=makeQuery(id+"F23.imprint","IMPRINT",FACE,{"disambiguationData":[TD([[makeQuery(id+"F23.imprint","IMPRINT",EDGE,{"derivedFrom":sQuery(id+"F23.wireOp",EDGE,"E20.bottom")}),-1.0]])]});
            var Q1;
            Q1=makeQuery(id+"F23.imprint","IMPRINT",FACE,{"disambiguationData":[TD([[makeQuery(id+"F23.imprint","IMPRINT",EDGE,{"derivedFrom":sQuery(id+"F23.wireOp",EDGE,"E19.bottom")}),-1.0]])]});
            extrude(context, id + "F24", {"entities" : qUnion([Q0, Q1]), "operationType" : NewBodyOperationType.ADD, "depth" : .5 * mm, "offsetDistance" : 25 * mm});
        }
        {
            var Q0;
            Q0=makeQuery(id+"F24.opExtrude","CAP_EDGE",EDGE,{"disambiguationData":[OSD([sQuery(id+"F23.wireOp",EDGE,"E20.top")])],"isStart":false});
            var Q1;
            Q1=makeQuery(id+"F24.opExtrude","CAP_EDGE",EDGE,{"disambiguationData":[OSD([sQuery(id+"F23.wireOp",EDGE,"E20.bottom")])],"isStart":false});
            var Q2;
            Q2=makeQuery(id+"F24.opExtrude","CAP_EDGE",EDGE,{"disambiguationData":[OSD([sQuery(id+"F23.wireOp",EDGE,"E19.top")])],"isStart":false});
            chamfer(context, id + "F25", {"entities" : qUnion([Q0, Q1, Q2]), "chamferType" : ChamferType.TWO_OFFSETS, "width1" : 7 * mm, "oppositeDirection" : false, "width2" : .5 * mm, "tangentPropagation" : true});
        }
        {
            var Q0;
            Q0=makeQuery(id+"F24.opExtrude","CAP_EDGE",EDGE,{"disambiguationData":[OSD([sQuery(id+"F23.wireOp",EDGE,"E19.bottom")])],"isStart":false});
            chamfer(context, id + "F26", {"entities" : qUnion([Q0]), "chamferType" : ChamferType.TWO_OFFSETS, "width1" : 7 * mm, "oppositeDirection" : true, "width2" : .5 * mm, "tangentPropagation" : true});
        }
        {
            var Q0;
            Q0=makeQuery(id+"F1.opExtrude","SWEPT_FACE",FACE,{"disambiguationData":[OSD([sQuery(id+"F0.wireOp",EDGE,"E10.2.59")])]});
            var sketch = newSketch(context, id + "F27", { "sketchPlane" : qUnion([Q0])});
            skLineSegment(sketch, "E21.bottom", {"start": v(116, 3.5) * mm, "end": v(113, 3.5) * mm});
            skLineSegment(sketch, "E21.top", {"start": v(116, 17.5) * mm, "end": v(113, 17.5) * mm});
            skLineSegment(sketch, "E21.left", {"start": v(116, 3.5) * mm, "end": v(116, 17.5) * mm});
            skLineSegment(sketch, "E21.right", {"start": v(113, 3.5) * mm, "end": v(113, 17.5) * mm});
            skPoint(sketch, "E21.middle", {"position": v(114.5, 10.5) * mm});
            skSolve(sketch);
        }
        {
            var Q0;
            Q0=makeQuery(id+"F27.imprint","IMPRINT",FACE,{"disambiguationData":[TD([[makeQuery(id+"F27.imprint","IMPRINT",EDGE,{"derivedFrom":sQuery(id+"F27.wireOp",EDGE,"E21.bottom")}),-1.0]])]});
            extrude(context, id + "F28", {"entities" : qUnion([Q0]), "operationType" : NewBodyOperationType.ADD, "depth" : .5 * mm, "offsetDistance" : 25 * mm});
        }
        {
            var Q0;
            Q0=makeQuery(id+"F28.opExtrude","CAP_EDGE",EDGE,{"disambiguationData":[OSD([sQuery(id+"F27.wireOp",EDGE,"E21.top")])],"isStart":false});
            var Q1;
            Q1=makeQuery(id+"F28.opExtrude","CAP_EDGE",EDGE,{"disambiguationData":[OSD([sQuery(id+"F27.wireOp",EDGE,"E21.bottom")])],"isStart":false});
            chamfer(context, id + "F29", {"entities" : qUnion([Q0, Q1]), "chamferType" : ChamferType.TWO_OFFSETS, "width1" : 7 * mm, "oppositeDirection" : false, "width2" : .5 * mm, "tangentPropagation" : true});
        }
        {
            var Q0;
            Q0=makeQuery(id+"F1.opExtrude","SWEPT_FACE",FACE,{"disambiguationData":[OSD([sQuery(id+"F0.wireOp",EDGE,"E10.2.20")])]});
            var sketch = newSketch(context, id + "F30", { "sketchPlane" : qUnion([Q0])});
            skLineSegment(sketch, "E22.bottom", {"start": v(148.9, 3.5) * mm, "end": v(145.9, 3.5) * mm});
            skLineSegment(sketch, "E22.top", {"start": v(148.9, 17.5) * mm, "end": v(145.9, 17.5) * mm});
            skLineSegment(sketch, "E22.left", {"start": v(148.9, 3.5) * mm, "end": v(148.9, 17.5) * mm});
            skLineSegment(sketch, "E22.right", {"start": v(145.9, 3.5) * mm, "end": v(145.9, 17.5) * mm});
            skPoint(sketch, "E22.middle", {"position": v(147.4, 10.5) * mm});
            skLineSegment(sketch, "E23.bottom", {"start": v(83.1, 3.5) * mm, "end": v(80.1, 3.5) * mm});
            skLineSegment(sketch, "E23.top", {"start": v(83.1, 17.5) * mm, "end": v(80.1, 17.5) * mm});
            skLineSegment(sketch, "E23.left", {"start": v(83.1, 3.5) * mm, "end": v(83.1, 17.5) * mm});
            skLineSegment(sketch, "E23.right", {"start": v(80.1, 3.5) * mm, "end": v(80.1, 17.5) * mm});
            skPoint(sketch, "E23.middle", {"position": v(81.6, 10.5) * mm});
            skSolve(sketch);
        }
        {
            var Q0;
            Q0=makeQuery(id+"F30.imprint","IMPRINT",FACE,{"disambiguationData":[TD([[makeQuery(id+"F30.imprint","IMPRINT",EDGE,{"derivedFrom":sQuery(id+"F30.wireOp",EDGE,"E23.bottom")}),-1.0]])]});
            var Q1;
            Q1=makeQuery(id+"F30.imprint","IMPRINT",FACE,{"disambiguationData":[TD([[makeQuery(id+"F30.imprint","IMPRINT",EDGE,{"derivedFrom":sQuery(id+"F30.wireOp",EDGE,"E22.bottom")}),-1.0]])]});
            extrude(context, id + "F31", {"entities" : qUnion([Q0, Q1]), "operationType" : NewBodyOperationType.ADD, "depth" : .5 * mm, "offsetDistance" : 25 * mm});
        }
        {
            var Q0;
            Q0=makeQuery(id+"F31.opExtrude","CAP_EDGE",EDGE,{"disambiguationData":[OSD([sQuery(id+"F30.wireOp",EDGE,"E23.top")])],"isStart":false});
            var Q1;
            Q1=makeQuery(id+"F31.opExtrude","CAP_EDGE",EDGE,{"disambiguationData":[OSD([sQuery(id+"F30.wireOp",EDGE,"E23.bottom")])],"isStart":false});
            var Q2;
            Q2=makeQuery(id+"F31.opExtrude","CAP_EDGE",EDGE,{"disambiguationData":[OSD([sQuery(id+"F30.wireOp",EDGE,"E22.top")])],"isStart":false});
            chamfer(context, id + "F32", {"entities" : qUnion([Q0, Q1, Q2]), "chamferType" : ChamferType.TWO_OFFSETS, "width1" : 7 * mm, "oppositeDirection" : false, "width2" : .5 * mm, "tangentPropagation" : true});
        }
        {
            var Q0;
            Q0=makeQuery(id+"F31.opExtrude","CAP_EDGE",EDGE,{"disambiguationData":[OSD([sQuery(id+"F30.wireOp",EDGE,"E22.bottom")])],"isStart":false});
            chamfer(context, id + "F33", {"entities" : qUnion([Q0]), "chamferType" : ChamferType.TWO_OFFSETS, "width1" : 7 * mm, "oppositeDirection" : true, "width2" : .5 * mm, "tangentPropagation" : true});
        }
        {
            var Q0;
            Q0=makeQuery(id+"F1.opExtrude","SWEPT_FACE",FACE,{"disambiguationData":[OSD([sQuery(id+"F0.wireOp",EDGE,"E10.2.45")])]});
            var sketch = newSketch(context, id + "F34", { "sketchPlane" : qUnion([Q0])});
            skLineSegment(sketch, "E24.bottom", {"start": v(116, 3.5) * mm, "end": v(113, 3.5) * mm});
            skLineSegment(sketch, "E24.top", {"start": v(116, 17.5) * mm, "end": v(113, 17.5) * mm});
            skLineSegment(sketch, "E24.left", {"start": v(116, 3.5) * mm, "end": v(116, 17.5) * mm});
            skLineSegment(sketch, "E24.right", {"start": v(113, 3.5) * mm, "end": v(113, 17.5) * mm});
            skPoint(sketch, "E24.middle", {"position": v(114.5, 10.5) * mm});
            skSolve(sketch);
        }
        {
            var Q0;
            Q0=makeQuery(id+"F34.imprint","IMPRINT",FACE,{"disambiguationData":[TD([[makeQuery(id+"F34.imprint","IMPRINT",EDGE,{"derivedFrom":sQuery(id+"F34.wireOp",EDGE,"E24.bottom")}),-1.0]])]});
            extrude(context, id + "F35", {"entities" : qUnion([Q0]), "operationType" : NewBodyOperationType.ADD, "depth" : .5 * mm, "offsetDistance" : 25 * mm});
        }
        {
            var Q0;
            Q0=makeQuery(id+"F35.opExtrude","CAP_EDGE",EDGE,{"disambiguationData":[OSD([sQuery(id+"F34.wireOp",EDGE,"E24.top")])],"isStart":false});
            var Q1;
            Q1=makeQuery(id+"F35.opExtrude","CAP_EDGE",EDGE,{"disambiguationData":[OSD([sQuery(id+"F34.wireOp",EDGE,"E24.bottom")])],"isStart":false});
            chamfer(context, id + "F36", {"entities" : qUnion([Q0, Q1]), "chamferType" : ChamferType.TWO_OFFSETS, "width1" : 7 * mm, "oppositeDirection" : false, "width2" : .5 * mm, "tangentPropagation" : true});
        }
        {
            var Q0;
            Q0=makeQuery(id+"F1.opExtrude","SWEPT_FACE",FACE,{"disambiguationData":[OSD([sQuery(id+"F0.wireOp",EDGE,"E10.1.44")])]});
            var sketch = newSketch(context, id + "F37", { "sketchPlane" : qUnion([Q0])});
            skLineSegment(sketch, "E25.bottom", {"start": v(-55.75, 3.5) * mm, "end": v(-58.75, 3.5) * mm});
            skLineSegment(sketch, "E25.top", {"start": v(-55.75, 17.5) * mm, "end": v(-58.75, 17.5) * mm});
            skLineSegment(sketch, "E25.left", {"start": v(-55.75, 3.5) * mm, "end": v(-55.75, 17.5) * mm});
            skLineSegment(sketch, "E25.right", {"start": v(-58.75, 3.5) * mm, "end": v(-58.75, 17.5) * mm});
            skPoint(sketch, "E25.middle", {"position": v(-57.25, 10.5) * mm});
            skSolve(sketch);
        }
        {
            var Q0;
            Q0=makeQuery(id+"F37.imprint","IMPRINT",FACE,{"disambiguationData":[TD([[makeQuery(id+"F37.imprint","IMPRINT",EDGE,{"derivedFrom":sQuery(id+"F37.wireOp",EDGE,"E25.bottom")}),-1.0]])]});
            extrude(context, id + "F38", {"entities" : qUnion([Q0]), "operationType" : NewBodyOperationType.ADD, "depth" : .5 * mm, "offsetDistance" : 25 * mm});
        }
        {
            var Q0;
            Q0=makeQuery(id+"F38.opExtrude","CAP_EDGE",EDGE,{"disambiguationData":[OSD([sQuery(id+"F37.wireOp",EDGE,"E25.top")])],"isStart":false});
            var Q1;
            Q1=makeQuery(id+"F38.opExtrude","CAP_EDGE",EDGE,{"disambiguationData":[OSD([sQuery(id+"F37.wireOp",EDGE,"E25.bottom")])],"isStart":false});
            chamfer(context, id + "F39", {"entities" : qUnion([Q0, Q1]), "chamferType" : ChamferType.TWO_OFFSETS, "width1" : 7 * mm, "oppositeDirection" : false, "width2" : .5 * mm, "tangentPropagation" : true});
        }
        {
            var Q0;
            Q0=makeQuery(id+"F1.opExtrude","SWEPT_FACE",FACE,{"disambiguationData":[OSD([sQuery(id+"F0.wireOp",EDGE,"E10.1.40")])]});
            var sketch = newSketch(context, id + "F40", { "sketchPlane" : qUnion([Q0])});
            skLineSegment(sketch, "E26.bottom", {"start": v(-22.84, 3.5) * mm, "end": v(-25.84, 3.5) * mm});
            skLineSegment(sketch, "E26.top", {"start": v(-22.84, 17.5) * mm, "end": v(-25.84, 17.5) * mm});
            skLineSegment(sketch, "E26.left", {"start": v(-22.84, 3.5) * mm, "end": v(-22.84, 17.5) * mm});
            skLineSegment(sketch, "E26.right", {"start": v(-25.84, 3.5) * mm, "end": v(-25.84, 17.5) * mm});
            skPoint(sketch, "E26.middle", {"position": v(-24.34, 10.5) * mm});
            skLineSegment(sketch, "E27.bottom", {"start": v(-88.66, 3.5) * mm, "end": v(-91.66, 3.5) * mm});
            skLineSegment(sketch, "E27.top", {"start": v(-88.66, 17.5) * mm, "end": v(-91.66, 17.5) * mm});
            skLineSegment(sketch, "E27.left", {"start": v(-88.66, 3.5) * mm, "end": v(-88.66, 17.5) * mm});
            skLineSegment(sketch, "E27.right", {"start": v(-91.66, 3.5) * mm, "end": v(-91.66, 17.5) * mm});
            skPoint(sketch, "E27.middle", {"position": v(-90.16, 10.5) * mm});
            skSolve(sketch);
        }
        {
            var Q0;
            Q0=makeQuery(id+"F40.imprint","IMPRINT",FACE,{"disambiguationData":[TD([[makeQuery(id+"F40.imprint","IMPRINT",EDGE,{"derivedFrom":sQuery(id+"F40.wireOp",EDGE,"E27.bottom")}),-1.0]])]});
            var Q1;
            Q1=makeQuery(id+"F40.imprint","IMPRINT",FACE,{"disambiguationData":[TD([[makeQuery(id+"F40.imprint","IMPRINT",EDGE,{"derivedFrom":sQuery(id+"F40.wireOp",EDGE,"E26.bottom")}),-1.0]])]});
            extrude(context, id + "F41", {"entities" : qUnion([Q0, Q1]), "operationType" : NewBodyOperationType.ADD, "depth" : .5 * mm, "offsetDistance" : 25 * mm});
        }
        {
            var Q0;
            Q0=makeQuery(id+"F41.opExtrude","CAP_EDGE",EDGE,{"disambiguationData":[OSD([sQuery(id+"F40.wireOp",EDGE,"E27.top")])],"isStart":false});
            var Q1;
            Q1=makeQuery(id+"F41.opExtrude","CAP_EDGE",EDGE,{"disambiguationData":[OSD([sQuery(id+"F40.wireOp",EDGE,"E27.bottom")])],"isStart":false});
            var Q2;
            Q2=makeQuery(id+"F41.opExtrude","CAP_EDGE",EDGE,{"disambiguationData":[OSD([sQuery(id+"F40.wireOp",EDGE,"E26.top")])],"isStart":false});
            chamfer(context, id + "F42", {"entities" : qUnion([Q0, Q1, Q2]), "chamferType" : ChamferType.TWO_OFFSETS, "width1" : 7 * mm, "oppositeDirection" : false, "width2" : .5 * mm, "tangentPropagation" : true});
        }
        {
            var Q0;
            Q0=makeQuery(id+"F41.opExtrude","CAP_EDGE",EDGE,{"disambiguationData":[OSD([sQuery(id+"F40.wireOp",EDGE,"E26.bottom")])],"isStart":false});
            chamfer(context, id + "F43", {"entities" : qUnion([Q0]), "chamferType" : ChamferType.TWO_OFFSETS, "width1" : 7 * mm, "oppositeDirection" : true, "width2" : .5 * mm, "tangentPropagation" : true});
        }
        {
            var Q0;
            Q0=makeQuery(id+"F1.opExtrude","SWEPT_FACE",FACE,{"disambiguationData":[OSD([sQuery(id+"F0.wireOp",EDGE,"E10.1.42")])]});
            var sketch = newSketch(context, id + "F44", { "sketchPlane" : qUnion([Q0])});
            skLineSegment(sketch, "E28.bottom", {"start": v(-55.75, 3.5) * mm, "end": v(-58.75, 3.5) * mm});
            skLineSegment(sketch, "E28.top", {"start": v(-55.75, 17.5) * mm, "end": v(-58.75, 17.5) * mm});
            skLineSegment(sketch, "E28.left", {"start": v(-55.75, 3.5) * mm, "end": v(-55.75, 17.5) * mm});
            skLineSegment(sketch, "E28.right", {"start": v(-58.75, 3.5) * mm, "end": v(-58.75, 17.5) * mm});
            skPoint(sketch, "E28.middle", {"position": v(-57.25, 10.5) * mm});
            skSolve(sketch);
        }
        {
            var Q0;
            Q0=makeQuery(id+"F44.imprint","IMPRINT",FACE,{"disambiguationData":[TD([[makeQuery(id+"F44.imprint","IMPRINT",EDGE,{"derivedFrom":sQuery(id+"F44.wireOp",EDGE,"E28.bottom")}),-1.0]])]});
            extrude(context, id + "F45", {"entities" : qUnion([Q0]), "operationType" : NewBodyOperationType.ADD, "depth" : .5 * mm, "offsetDistance" : 25 * mm});
        }
        {
            var Q0;
            Q0=makeQuery(id+"F45.opExtrude","CAP_EDGE",EDGE,{"disambiguationData":[OSD([sQuery(id+"F44.wireOp",EDGE,"E28.top")])],"isStart":false});
            var Q1;
            Q1=makeQuery(id+"F45.opExtrude","CAP_EDGE",EDGE,{"disambiguationData":[OSD([sQuery(id+"F44.wireOp",EDGE,"E28.bottom")])],"isStart":false});
            chamfer(context, id + "F46", {"entities" : qUnion([Q0, Q1]), "chamferType" : ChamferType.TWO_OFFSETS, "width1" : 7 * mm, "oppositeDirection" : false, "width2" : .5 * mm, "tangentPropagation" : true});
        }
        {
            var Q0;
            Q0=makeQuery(id+"F1.opExtrude","SWEPT_FACE",FACE,{"disambiguationData":[OSD([sQuery(id+"F0.wireOp",EDGE,"E10.1.52")])]});
            var sketch = newSketch(context, id + "F47", { "sketchPlane" : qUnion([Q0])});
            skLineSegment(sketch, "E29.bottom", {"start": v(-22.84, 3.5) * mm, "end": v(-25.84, 3.5) * mm});
            skLineSegment(sketch, "E29.top", {"start": v(-22.84, 17.5) * mm, "end": v(-25.84, 17.5) * mm});
            skLineSegment(sketch, "E29.left", {"start": v(-22.84, 3.5) * mm, "end": v(-22.84, 17.5) * mm});
            skLineSegment(sketch, "E29.right", {"start": v(-25.84, 3.5) * mm, "end": v(-25.84, 17.5) * mm});
            skPoint(sketch, "E29.middle", {"position": v(-24.34, 10.5) * mm});
            skLineSegment(sketch, "E30.bottom", {"start": v(-88.66, 3.5) * mm, "end": v(-91.66, 3.5) * mm});
            skLineSegment(sketch, "E30.top", {"start": v(-88.66, 17.5) * mm, "end": v(-91.66, 17.5) * mm});
            skLineSegment(sketch, "E30.left", {"start": v(-88.66, 3.5) * mm, "end": v(-88.66, 17.5) * mm});
            skLineSegment(sketch, "E30.right", {"start": v(-91.66, 3.5) * mm, "end": v(-91.66, 17.5) * mm});
            skPoint(sketch, "E30.middle", {"position": v(-90.16, 10.5) * mm});
            skSolve(sketch);
        }
        {
            var Q0;
            Q0=makeQuery(id+"F47.imprint","IMPRINT",FACE,{"disambiguationData":[TD([[makeQuery(id+"F47.imprint","IMPRINT",EDGE,{"derivedFrom":sQuery(id+"F47.wireOp",EDGE,"E30.bottom")}),-1.0]])]});
            var Q1;
            Q1=makeQuery(id+"F47.imprint","IMPRINT",FACE,{"disambiguationData":[TD([[makeQuery(id+"F47.imprint","IMPRINT",EDGE,{"derivedFrom":sQuery(id+"F47.wireOp",EDGE,"E29.bottom")}),-1.0]])]});
            extrude(context, id + "F48", {"entities" : qUnion([Q0, Q1]), "operationType" : NewBodyOperationType.ADD, "depth" : .5 * mm, "offsetDistance" : 25 * mm});
        }
        {
            var Q0;
            Q0=makeQuery(id+"F48.opExtrude","CAP_EDGE",EDGE,{"disambiguationData":[OSD([sQuery(id+"F47.wireOp",EDGE,"E30.top")])],"isStart":false});
            var Q1;
            Q1=makeQuery(id+"F48.opExtrude","CAP_EDGE",EDGE,{"disambiguationData":[OSD([sQuery(id+"F47.wireOp",EDGE,"E30.bottom")])],"isStart":false});
            var Q2;
            Q2=makeQuery(id+"F48.opExtrude","CAP_EDGE",EDGE,{"disambiguationData":[OSD([sQuery(id+"F47.wireOp",EDGE,"E29.top")])],"isStart":false});
            chamfer(context, id + "F49", {"entities" : qUnion([Q0, Q1, Q2]), "chamferType" : ChamferType.TWO_OFFSETS, "width1" : 7 * mm, "oppositeDirection" : false, "width2" : .5 * mm, "tangentPropagation" : true});
        }
        {
            var Q0;
            Q0=makeQuery(id+"F48.opExtrude","CAP_EDGE",EDGE,{"disambiguationData":[OSD([sQuery(id+"F47.wireOp",EDGE,"E29.bottom")])],"isStart":false});
            chamfer(context, id + "F50", {"entities" : qUnion([Q0]), "chamferType" : ChamferType.TWO_OFFSETS, "width1" : 7 * mm, "oppositeDirection" : true, "width2" : .5 * mm, "tangentPropagation" : true});
        }
        {
            var Q0;
            Q0=makeQuery(id+"F1.opExtrude","SWEPT_FACE",FACE,{"disambiguationData":[OSD([sQuery(id+"F0.wireOp",EDGE,"E10.1.49")])]});
            var sketch = newSketch(context, id + "F51", { "sketchPlane" : qUnion([Q0])});
            skLineSegment(sketch, "E31.bottom", {"start": v(-55.75, 3.5) * mm, "end": v(-58.75, 3.5) * mm});
            skLineSegment(sketch, "E31.top", {"start": v(-55.75, 17.5) * mm, "end": v(-58.75, 17.5) * mm});
            skLineSegment(sketch, "E31.left", {"start": v(-55.75, 3.5) * mm, "end": v(-55.75, 17.5) * mm});
            skLineSegment(sketch, "E31.right", {"start": v(-58.75, 3.5) * mm, "end": v(-58.75, 17.5) * mm});
            skPoint(sketch, "E31.middle", {"position": v(-57.25, 10.5) * mm});
            skSolve(sketch);
        }
        {
            var Q0;
            Q0=makeQuery(id+"F51.imprint","IMPRINT",FACE,{"disambiguationData":[TD([[makeQuery(id+"F51.imprint","IMPRINT",EDGE,{"derivedFrom":sQuery(id+"F51.wireOp",EDGE,"E31.bottom")}),-1.0]])]});
            extrude(context, id + "F52", {"entities" : qUnion([Q0]), "operationType" : NewBodyOperationType.ADD, "depth" : .5 * mm, "offsetDistance" : 25 * mm});
        }
        {
            var Q0;
            Q0=makeQuery(id+"F52.opExtrude","CAP_EDGE",EDGE,{"disambiguationData":[OSD([sQuery(id+"F51.wireOp",EDGE,"E31.top")])],"isStart":false});
            var Q1;
            Q1=makeQuery(id+"F52.opExtrude","CAP_EDGE",EDGE,{"disambiguationData":[OSD([sQuery(id+"F51.wireOp",EDGE,"E31.bottom")])],"isStart":false});
            chamfer(context, id + "F53", {"entities" : qUnion([Q0, Q1]), "chamferType" : ChamferType.TWO_OFFSETS, "width1" : 7 * mm, "oppositeDirection" : false, "width2" : .5 * mm, "tangentPropagation" : true});
        }
        {
            var Q0;
            Q0=makeQuery(id+"F1.opExtrude","SWEPT_FACE",FACE,{"disambiguationData":[OSD([sQuery(id+"F0.wireOp",EDGE,"E10.1.43")])]});
            var sketch = newSketch(context, id + "F54", { "sketchPlane" : qUnion([Q0])});
            skLineSegment(sketch, "E32.bottom", {"start": v(-55.75, 3.5) * mm, "end": v(-58.75, 3.5) * mm});
            skLineSegment(sketch, "E32.top", {"start": v(-55.75, 17.5) * mm, "end": v(-58.75, 17.5) * mm});
            skLineSegment(sketch, "E32.left", {"start": v(-55.75, 3.5) * mm, "end": v(-55.75, 17.5) * mm});
            skLineSegment(sketch, "E32.right", {"start": v(-58.75, 3.5) * mm, "end": v(-58.75, 17.5) * mm});
            skPoint(sketch, "E32.middle", {"position": v(-57.25, 10.5) * mm});
            skSolve(sketch);
        }
        {
            var Q0;
            Q0=makeQuery(id+"F54.imprint","IMPRINT",FACE,{"disambiguationData":[TD([[makeQuery(id+"F54.imprint","IMPRINT",EDGE,{"derivedFrom":sQuery(id+"F54.wireOp",EDGE,"E32.bottom")}),-1.0]])]});
            extrude(context, id + "F55", {"entities" : qUnion([Q0]), "operationType" : NewBodyOperationType.ADD, "depth" : .5 * mm, "offsetDistance" : 25 * mm});
        }
        {
            var Q0;
            Q0=makeQuery(id+"F55.opExtrude","CAP_EDGE",EDGE,{"disambiguationData":[OSD([sQuery(id+"F54.wireOp",EDGE,"E32.top")])],"isStart":false});
            var Q1;
            Q1=makeQuery(id+"F55.opExtrude","CAP_EDGE",EDGE,{"disambiguationData":[OSD([sQuery(id+"F54.wireOp",EDGE,"E32.bottom")])],"isStart":false});
            chamfer(context, id + "F56", {"entities" : qUnion([Q0, Q1]), "chamferType" : ChamferType.TWO_OFFSETS, "width1" : 7 * mm, "oppositeDirection" : false, "width2" : .5 * mm, "tangentPropagation" : true});
        }
        {
            var Q0;
            Q0=makeQuery(id+"F1.opExtrude","SWEPT_FACE",FACE,{"disambiguationData":[OSD([sQuery(id+"F0.wireOp",EDGE,"E10.1.33")])]});
            var sketch = newSketch(context, id + "F57", { "sketchPlane" : qUnion([Q0])});
            skLineSegment(sketch, "E33.bottom", {"start": v(-22.84, 3.5) * mm, "end": v(-25.84, 3.5) * mm});
            skLineSegment(sketch, "E33.top", {"start": v(-22.84, 17.5) * mm, "end": v(-25.84, 17.5) * mm});
            skLineSegment(sketch, "E33.left", {"start": v(-22.84, 3.5) * mm, "end": v(-22.84, 17.5) * mm});
            skLineSegment(sketch, "E33.right", {"start": v(-25.84, 3.5) * mm, "end": v(-25.84, 17.5) * mm});
            skPoint(sketch, "E33.middle", {"position": v(-24.34, 10.5) * mm});
            skLineSegment(sketch, "E34.bottom", {"start": v(-88.66, 3.5) * mm, "end": v(-91.66, 3.5) * mm});
            skLineSegment(sketch, "E34.top", {"start": v(-88.66, 17.5) * mm, "end": v(-91.66, 17.5) * mm});
            skLineSegment(sketch, "E34.left", {"start": v(-88.66, 3.5) * mm, "end": v(-88.66, 17.5) * mm});
            skLineSegment(sketch, "E34.right", {"start": v(-91.66, 3.5) * mm, "end": v(-91.66, 17.5) * mm});
            skPoint(sketch, "E34.middle", {"position": v(-90.16, 10.5) * mm});
            skSolve(sketch);
        }
        {
            var Q0;
            Q0=makeQuery(id+"F57.imprint","IMPRINT",FACE,{"disambiguationData":[TD([[makeQuery(id+"F57.imprint","IMPRINT",EDGE,{"derivedFrom":sQuery(id+"F57.wireOp",EDGE,"E34.bottom")}),-1.0]])]});
            var Q1;
            Q1=makeQuery(id+"F57.imprint","IMPRINT",FACE,{"disambiguationData":[TD([[makeQuery(id+"F57.imprint","IMPRINT",EDGE,{"derivedFrom":sQuery(id+"F57.wireOp",EDGE,"E33.bottom")}),-1.0]])]});
            extrude(context, id + "F58", {"entities" : qUnion([Q0, Q1]), "operationType" : NewBodyOperationType.ADD, "depth" : .5 * mm, "offsetDistance" : 25 * mm});
        }
        {
            var Q0;
            Q0=makeQuery(id+"F58.opExtrude","CAP_EDGE",EDGE,{"disambiguationData":[OSD([sQuery(id+"F57.wireOp",EDGE,"E34.top")])],"isStart":false});
            var Q1;
            Q1=makeQuery(id+"F58.opExtrude","CAP_EDGE",EDGE,{"disambiguationData":[OSD([sQuery(id+"F57.wireOp",EDGE,"E34.bottom")])],"isStart":false});
            var Q2;
            Q2=makeQuery(id+"F58.opExtrude","CAP_EDGE",EDGE,{"disambiguationData":[OSD([sQuery(id+"F57.wireOp",EDGE,"E33.top")])],"isStart":false});
            chamfer(context, id + "F59", {"entities" : qUnion([Q0, Q1, Q2]), "chamferType" : ChamferType.TWO_OFFSETS, "width1" : 7 * mm, "oppositeDirection" : false, "width2" : .5 * mm, "tangentPropagation" : true});
        }
        {
            var Q0;
            Q0=makeQuery(id+"F58.opExtrude","CAP_EDGE",EDGE,{"disambiguationData":[OSD([sQuery(id+"F57.wireOp",EDGE,"E33.bottom")])],"isStart":false});
            chamfer(context, id + "F60", {"entities" : qUnion([Q0]), "chamferType" : ChamferType.TWO_OFFSETS, "width1" : 7 * mm, "oppositeDirection" : true, "width2" : .5 * mm, "tangentPropagation" : true});
        }
        {
            var Q0;
            Q0=makeQuery(id+"F1.opExtrude","SWEPT_FACE",FACE,{"disambiguationData":[OSD([sQuery(id+"F0.wireOp",EDGE,"E10.1.46")])]});
            var sketch = newSketch(context, id + "F61", { "sketchPlane" : qUnion([Q0])});
            skLineSegment(sketch, "E35.bottom", {"start": v(-55.75, 3.5) * mm, "end": v(-58.75, 3.5) * mm});
            skLineSegment(sketch, "E35.top", {"start": v(-55.75, 17.5) * mm, "end": v(-58.75, 17.5) * mm});
            skLineSegment(sketch, "E35.left", {"start": v(-55.75, 3.5) * mm, "end": v(-55.75, 17.5) * mm});
            skLineSegment(sketch, "E35.right", {"start": v(-58.75, 3.5) * mm, "end": v(-58.75, 17.5) * mm});
            skPoint(sketch, "E35.middle", {"position": v(-57.25, 10.5) * mm});
            skSolve(sketch);
        }
        {
            var Q0;
            Q0=makeQuery(id+"F61.imprint","IMPRINT",FACE,{"disambiguationData":[TD([[makeQuery(id+"F61.imprint","IMPRINT",EDGE,{"derivedFrom":sQuery(id+"F61.wireOp",EDGE,"E35.bottom")}),-1.0]])]});
            extrude(context, id + "F62", {"entities" : qUnion([Q0]), "operationType" : NewBodyOperationType.ADD, "depth" : .5 * mm, "offsetDistance" : 25 * mm});
        }
        {
            var Q0;
            Q0=makeQuery(id+"F62.opExtrude","CAP_EDGE",EDGE,{"disambiguationData":[OSD([sQuery(id+"F61.wireOp",EDGE,"E35.top")])],"isStart":false});
            var Q1;
            Q1=makeQuery(id+"F62.opExtrude","CAP_EDGE",EDGE,{"disambiguationData":[OSD([sQuery(id+"F61.wireOp",EDGE,"E35.bottom")])],"isStart":false});
            chamfer(context, id + "F63", {"entities" : qUnion([Q0, Q1]), "chamferType" : ChamferType.TWO_OFFSETS, "width1" : 7 * mm, "oppositeDirection" : false, "width2" : .5 * mm, "tangentPropagation" : true});
        }
        {
            var Q0;
            Q0=makeQuery(id+"F1.opExtrude","SWEPT_FACE",FACE,{"disambiguationData":[OSD([sQuery(id+"F0.wireOp",EDGE,"E10.1.28")])]});
            var sketch = newSketch(context, id + "F64", { "sketchPlane" : qUnion([Q0])});
            skLineSegment(sketch, "E36.bottom", {"start": v(-22.84, 3.5) * mm, "end": v(-25.84, 3.5) * mm});
            skLineSegment(sketch, "E36.top", {"start": v(-22.84, 17.5) * mm, "end": v(-25.84, 17.5) * mm});
            skLineSegment(sketch, "E36.left", {"start": v(-22.84, 3.5) * mm, "end": v(-22.84, 17.5) * mm});
            skLineSegment(sketch, "E36.right", {"start": v(-25.84, 3.5) * mm, "end": v(-25.84, 17.5) * mm});
            skPoint(sketch, "E36.middle", {"position": v(-24.34, 10.5) * mm});
            skLineSegment(sketch, "E37.bottom", {"start": v(-88.66, 3.5) * mm, "end": v(-91.66, 3.5) * mm});
            skLineSegment(sketch, "E37.top", {"start": v(-88.66, 17.5) * mm, "end": v(-91.66, 17.5) * mm});
            skLineSegment(sketch, "E37.left", {"start": v(-88.66, 3.5) * mm, "end": v(-88.66, 17.5) * mm});
            skLineSegment(sketch, "E37.right", {"start": v(-91.66, 3.5) * mm, "end": v(-91.66, 17.5) * mm});
            skPoint(sketch, "E37.middle", {"position": v(-90.16, 10.5) * mm});
            skSolve(sketch);
        }
        {
            var Q0;
            Q0=makeQuery(id+"F64.imprint","IMPRINT",FACE,{"disambiguationData":[TD([[makeQuery(id+"F64.imprint","IMPRINT",EDGE,{"derivedFrom":sQuery(id+"F64.wireOp",EDGE,"E37.bottom")}),-1.0]])]});
            var Q1;
            Q1=makeQuery(id+"F64.imprint","IMPRINT",FACE,{"disambiguationData":[TD([[makeQuery(id+"F64.imprint","IMPRINT",EDGE,{"derivedFrom":sQuery(id+"F64.wireOp",EDGE,"E36.bottom")}),-1.0]])]});
            extrude(context, id + "F65", {"entities" : qUnion([Q0, Q1]), "operationType" : NewBodyOperationType.ADD, "depth" : .5 * mm, "offsetDistance" : 25 * mm});
        }
        {
            var Q0;
            Q0=makeQuery(id+"F65.opExtrude","CAP_EDGE",EDGE,{"disambiguationData":[OSD([sQuery(id+"F64.wireOp",EDGE,"E37.top")])],"isStart":false});
            var Q1;
            Q1=makeQuery(id+"F65.opExtrude","CAP_EDGE",EDGE,{"disambiguationData":[OSD([sQuery(id+"F64.wireOp",EDGE,"E37.bottom")])],"isStart":false});
            var Q2;
            Q2=makeQuery(id+"F65.opExtrude","CAP_EDGE",EDGE,{"disambiguationData":[OSD([sQuery(id+"F64.wireOp",EDGE,"E36.top")])],"isStart":false});
            chamfer(context, id + "F66", {"entities" : qUnion([Q0, Q1, Q2]), "chamferType" : ChamferType.TWO_OFFSETS, "width1" : 7 * mm, "oppositeDirection" : false, "width2" : .5 * mm, "tangentPropagation" : true});
        }
        {
            var Q0;
            Q0=makeQuery(id+"F65.opExtrude","CAP_EDGE",EDGE,{"disambiguationData":[OSD([sQuery(id+"F64.wireOp",EDGE,"E36.bottom")])],"isStart":false});
            chamfer(context, id + "F67", {"entities" : qUnion([Q0]), "chamferType" : ChamferType.TWO_OFFSETS, "width1" : 7 * mm, "oppositeDirection" : true, "width2" : .5 * mm, "tangentPropagation" : true});
        }
        {
            var Q0;
            Q0=makeQuery(id+"F1.opExtrude","SWEPT_FACE",FACE,{"disambiguationData":[OSD([sQuery(id+"F0.wireOp",EDGE,"E10.1.47")])]});
            var sketch = newSketch(context, id + "F68", { "sketchPlane" : qUnion([Q0])});
            skLineSegment(sketch, "E38.bottom", {"start": v(-55.75, 3.5) * mm, "end": v(-58.75, 3.5) * mm});
            skLineSegment(sketch, "E38.top", {"start": v(-55.75, 17.5) * mm, "end": v(-58.75, 17.5) * mm});
            skLineSegment(sketch, "E38.left", {"start": v(-55.75, 3.5) * mm, "end": v(-55.75, 17.5) * mm});
            skLineSegment(sketch, "E38.right", {"start": v(-58.75, 3.5) * mm, "end": v(-58.75, 17.5) * mm});
            skPoint(sketch, "E38.middle", {"position": v(-57.25, 10.5) * mm});
            skSolve(sketch);
        }
        {
            var Q0;
            Q0=makeQuery(id+"F68.imprint","IMPRINT",FACE,{"disambiguationData":[TD([[makeQuery(id+"F68.imprint","IMPRINT",EDGE,{"derivedFrom":sQuery(id+"F68.wireOp",EDGE,"E38.bottom")}),-1.0]])]});
            extrude(context, id + "F69", {"entities" : qUnion([Q0]), "operationType" : NewBodyOperationType.ADD, "depth" : .5 * mm, "offsetDistance" : 25 * mm});
        }
        {
            var Q0;
            Q0=makeQuery(id+"F69.opExtrude","CAP_EDGE",EDGE,{"disambiguationData":[OSD([sQuery(id+"F68.wireOp",EDGE,"E38.top")])],"isStart":false});
            var Q1;
            Q1=makeQuery(id+"F69.opExtrude","CAP_EDGE",EDGE,{"disambiguationData":[OSD([sQuery(id+"F68.wireOp",EDGE,"E38.bottom")])],"isStart":false});
            chamfer(context, id + "F70", {"entities" : qUnion([Q0, Q1]), "chamferType" : ChamferType.TWO_OFFSETS, "width1" : 7 * mm, "oppositeDirection" : false, "width2" : .5 * mm, "tangentPropagation" : true});
        }
        {
            var Q0;
            Q0=makeQuery(id+"F1.opExtrude","SWEPT_FACE",FACE,{"disambiguationData":[OSD([sQuery(id+"F0.wireOp",EDGE,"E5.2")])]});
            var sketch = newSketch(context, id + "F71", { "sketchPlane" : qUnion([Q0])});
            skLineSegment(sketch, "E39.bottom", {"start": v(116, 3.5) * mm, "end": v(113, 3.5) * mm});
            skLineSegment(sketch, "E39.top", {"start": v(116, 17.5) * mm, "end": v(113, 17.5) * mm});
            skLineSegment(sketch, "E39.left", {"start": v(116, 3.5) * mm, "end": v(116, 17.5) * mm});
            skLineSegment(sketch, "E39.right", {"start": v(113, 3.5) * mm, "end": v(113, 17.5) * mm});
            skPoint(sketch, "E39.middle", {"position": v(114.5, 10.5) * mm});
            skSolve(sketch);
        }
        {
            var Q0;
            Q0=makeQuery(id+"F71.imprint","IMPRINT",FACE,{"disambiguationData":[TD([[makeQuery(id+"F71.imprint","IMPRINT",EDGE,{"derivedFrom":sQuery(id+"F71.wireOp",EDGE,"E39.bottom")}),-1.0]])]});
            extrude(context, id + "F72", {"entities" : qUnion([Q0]), "operationType" : NewBodyOperationType.ADD, "depth" : .5 * mm, "offsetDistance" : 25 * mm});
        }
        {
            var Q0;
            Q0=makeQuery(id+"F72.opExtrude","CAP_EDGE",EDGE,{"disambiguationData":[OSD([sQuery(id+"F71.wireOp",EDGE,"E39.top")])],"isStart":false});
            var Q1;
            Q1=makeQuery(id+"F72.opExtrude","CAP_EDGE",EDGE,{"disambiguationData":[OSD([sQuery(id+"F71.wireOp",EDGE,"E39.bottom")])],"isStart":false});
            chamfer(context, id + "F73", {"entities" : qUnion([Q0, Q1]), "chamferType" : ChamferType.TWO_OFFSETS, "width1" : 7 * mm, "oppositeDirection" : false, "width2" : .5 * mm, "tangentPropagation" : true});
        }
        {
            var Q0;
            Q0=makeQuery(id+"F1.opExtrude","SWEPT_FACE",FACE,{"disambiguationData":[OSD([sQuery(id+"F0.wireOp",EDGE,"E7.2")])]});
            var sketch = newSketch(context, id + "F74", { "sketchPlane" : qUnion([Q0])});
            skLineSegment(sketch, "E40.bottom", {"start": v(148.9, 3.5) * mm, "end": v(145.9, 3.5) * mm});
            skLineSegment(sketch, "E40.top", {"start": v(148.9, 17.5) * mm, "end": v(145.9, 17.5) * mm});
            skLineSegment(sketch, "E40.left", {"start": v(148.9, 3.5) * mm, "end": v(148.9, 17.5) * mm});
            skLineSegment(sketch, "E40.right", {"start": v(145.9, 3.5) * mm, "end": v(145.9, 17.5) * mm});
            skPoint(sketch, "E40.middle", {"position": v(147.4, 10.5) * mm});
            skLineSegment(sketch, "E41.bottom", {"start": v(83.1, 3.5) * mm, "end": v(80.1, 3.5) * mm});
            skLineSegment(sketch, "E41.top", {"start": v(83.1, 17.5) * mm, "end": v(80.1, 17.5) * mm});
            skLineSegment(sketch, "E41.left", {"start": v(83.1, 3.5) * mm, "end": v(83.1, 17.5) * mm});
            skLineSegment(sketch, "E41.right", {"start": v(80.1, 3.5) * mm, "end": v(80.1, 17.5) * mm});
            skPoint(sketch, "E41.middle", {"position": v(81.6, 10.5) * mm});
            skSolve(sketch);
        }
        {
            var Q0;
            Q0=makeQuery(id+"F74.imprint","IMPRINT",FACE,{"disambiguationData":[TD([[makeQuery(id+"F74.imprint","IMPRINT",EDGE,{"derivedFrom":sQuery(id+"F74.wireOp",EDGE,"E41.bottom")}),-1.0]])]});
            var Q1;
            Q1=makeQuery(id+"F74.imprint","IMPRINT",FACE,{"disambiguationData":[TD([[makeQuery(id+"F74.imprint","IMPRINT",EDGE,{"derivedFrom":sQuery(id+"F74.wireOp",EDGE,"E40.bottom")}),-1.0]])]});
            extrude(context, id + "F75", {"entities" : qUnion([Q0, Q1]), "operationType" : NewBodyOperationType.ADD, "depth" : .5 * mm, "offsetDistance" : 25 * mm});
        }
        {
            var Q0;
            Q0=makeQuery(id+"F75.opExtrude","CAP_EDGE",EDGE,{"disambiguationData":[OSD([sQuery(id+"F74.wireOp",EDGE,"E41.top")])],"isStart":false});
            var Q1;
            Q1=makeQuery(id+"F75.opExtrude","CAP_EDGE",EDGE,{"disambiguationData":[OSD([sQuery(id+"F74.wireOp",EDGE,"E41.bottom")])],"isStart":false});
            var Q2;
            Q2=makeQuery(id+"F75.opExtrude","CAP_EDGE",EDGE,{"disambiguationData":[OSD([sQuery(id+"F74.wireOp",EDGE,"E40.top")])],"isStart":false});
            chamfer(context, id + "F76", {"entities" : qUnion([Q0, Q1, Q2]), "chamferType" : ChamferType.TWO_OFFSETS, "width1" : 7 * mm, "oppositeDirection" : false, "width2" : .5 * mm, "tangentPropagation" : true});
        }
        {
            var Q0;
            Q0=makeQuery(id+"F75.opExtrude","CAP_EDGE",EDGE,{"disambiguationData":[OSD([sQuery(id+"F74.wireOp",EDGE,"E40.bottom")])],"isStart":false});
            chamfer(context, id + "F77", {"entities" : qUnion([Q0]), "chamferType" : ChamferType.TWO_OFFSETS, "width1" : 7 * mm, "oppositeDirection" : true, "width2" : .5 * mm, "tangentPropagation" : true});
        }
        {
            var Q0;
            Q0=makeQuery(id+"F1.opExtrude","SWEPT_FACE",FACE,{"disambiguationData":[OSD([sQuery(id+"F0.wireOp",EDGE,"E4.2")])]});
            var sketch = newSketch(context, id + "F78", { "sketchPlane" : qUnion([Q0])});
            skLineSegment(sketch, "E42.bottom", {"start": v(116, 3.5) * mm, "end": v(113, 3.5) * mm});
            skLineSegment(sketch, "E42.top", {"start": v(116, 17.5) * mm, "end": v(113, 17.5) * mm});
            skLineSegment(sketch, "E42.left", {"start": v(116, 3.5) * mm, "end": v(116, 17.5) * mm});
            skLineSegment(sketch, "E42.right", {"start": v(113, 3.5) * mm, "end": v(113, 17.5) * mm});
            skPoint(sketch, "E42.middle", {"position": v(114.5, 10.5) * mm});
            skSolve(sketch);
        }
        {
            var Q0;
            Q0=makeQuery(id+"F78.imprint","IMPRINT",FACE,{"disambiguationData":[TD([[makeQuery(id+"F78.imprint","IMPRINT",EDGE,{"derivedFrom":sQuery(id+"F78.wireOp",EDGE,"E42.bottom")}),-1.0]])]});
            extrude(context, id + "F79", {"entities" : qUnion([Q0]), "operationType" : NewBodyOperationType.ADD, "depth" : .5 * mm, "offsetDistance" : 25 * mm});
        }
        {
            var Q0;
            Q0=makeQuery(id+"F79.opExtrude","CAP_EDGE",EDGE,{"disambiguationData":[OSD([sQuery(id+"F78.wireOp",EDGE,"E42.top")])],"isStart":false});
            var Q1;
            Q1=makeQuery(id+"F79.opExtrude","CAP_EDGE",EDGE,{"disambiguationData":[OSD([sQuery(id+"F78.wireOp",EDGE,"E42.bottom")])],"isStart":false});
            chamfer(context, id + "F80", {"entities" : qUnion([Q0, Q1]), "chamferType" : ChamferType.TWO_OFFSETS, "width1" : 7 * mm, "oppositeDirection" : false, "width2" : .5 * mm, "tangentPropagation" : true});
        }
        {
            var Q0;
            Q0=makeQuery(id+"F1.opExtrude","SWEPT_FACE",FACE,{"disambiguationData":[OSD([sQuery(id+"F0.wireOp",EDGE,"E8.2")])]});
            var sketch = newSketch(context, id + "F81", { "sketchPlane" : qUnion([Q0])});
            skLineSegment(sketch, "E43.bottom", {"start": v(148.9, 3.5) * mm, "end": v(145.9, 3.5) * mm});
            skLineSegment(sketch, "E43.top", {"start": v(148.9, 17.5) * mm, "end": v(145.9, 17.5) * mm});
            skLineSegment(sketch, "E43.left", {"start": v(148.9, 3.5) * mm, "end": v(148.9, 17.5) * mm});
            skLineSegment(sketch, "E43.right", {"start": v(145.9, 3.5) * mm, "end": v(145.9, 17.5) * mm});
            skPoint(sketch, "E43.middle", {"position": v(147.4, 10.5) * mm});
            skLineSegment(sketch, "E44.bottom", {"start": v(83.1, 3.5) * mm, "end": v(80.1, 3.5) * mm});
            skLineSegment(sketch, "E44.top", {"start": v(83.1, 17.5) * mm, "end": v(80.1, 17.5) * mm});
            skLineSegment(sketch, "E44.left", {"start": v(83.1, 3.5) * mm, "end": v(83.1, 17.5) * mm});
            skLineSegment(sketch, "E44.right", {"start": v(80.1, 3.5) * mm, "end": v(80.1, 17.5) * mm});
            skPoint(sketch, "E44.middle", {"position": v(81.6, 10.5) * mm});
            skSolve(sketch);
        }
        {
            var Q0;
            Q0=makeQuery(id+"F81.imprint","IMPRINT",FACE,{"disambiguationData":[TD([[makeQuery(id+"F81.imprint","IMPRINT",EDGE,{"derivedFrom":sQuery(id+"F81.wireOp",EDGE,"E44.bottom")}),-1.0]])]});
            var Q1;
            Q1=makeQuery(id+"F81.imprint","IMPRINT",FACE,{"disambiguationData":[TD([[makeQuery(id+"F81.imprint","IMPRINT",EDGE,{"derivedFrom":sQuery(id+"F81.wireOp",EDGE,"E43.bottom")}),-1.0]])]});
            extrude(context, id + "F82", {"entities" : qUnion([Q0, Q1]), "operationType" : NewBodyOperationType.ADD, "depth" : .5 * mm, "offsetDistance" : 25 * mm});
        }
        {
            var Q0;
            Q0=makeQuery(id+"F82.opExtrude","CAP_EDGE",EDGE,{"disambiguationData":[OSD([sQuery(id+"F81.wireOp",EDGE,"E44.top")])],"isStart":false});
            var Q1;
            Q1=makeQuery(id+"F82.opExtrude","CAP_EDGE",EDGE,{"disambiguationData":[OSD([sQuery(id+"F81.wireOp",EDGE,"E44.bottom")])],"isStart":false});
            var Q2;
            Q2=makeQuery(id+"F82.opExtrude","CAP_EDGE",EDGE,{"disambiguationData":[OSD([sQuery(id+"F81.wireOp",EDGE,"E43.top")])],"isStart":false});
            chamfer(context, id + "F83", {"entities" : qUnion([Q0, Q1, Q2]), "chamferType" : ChamferType.TWO_OFFSETS, "width1" : 7 * mm, "oppositeDirection" : false, "width2" : .5 * mm, "tangentPropagation" : true});
        }
        {
            var Q0;
            Q0=makeQuery(id+"F82.opExtrude","CAP_EDGE",EDGE,{"disambiguationData":[OSD([sQuery(id+"F81.wireOp",EDGE,"E43.bottom")])],"isStart":false});
            chamfer(context, id + "F84", {"entities" : qUnion([Q0]), "chamferType" : ChamferType.TWO_OFFSETS, "width1" : 7 * mm, "oppositeDirection" : true, "width2" : .5 * mm, "tangentPropagation" : true});
        }
        {
            var Q0;
            Q0=makeQuery(id+"F1.opExtrude","SWEPT_FACE",FACE,{"disambiguationData":[OSD([sQuery(id+"F0.wireOp",EDGE,"E6.2")])]});
            var sketch = newSketch(context, id + "F85", { "sketchPlane" : qUnion([Q0])});
            skLineSegment(sketch, "E45.bottom", {"start": v(116, 3.5) * mm, "end": v(113, 3.5) * mm});
            skLineSegment(sketch, "E45.top", {"start": v(116, 17.5) * mm, "end": v(113, 17.5) * mm});
            skLineSegment(sketch, "E45.left", {"start": v(116, 3.5) * mm, "end": v(116, 17.5) * mm});
            skLineSegment(sketch, "E45.right", {"start": v(113, 3.5) * mm, "end": v(113, 17.5) * mm});
            skPoint(sketch, "E45.middle", {"position": v(114.5, 10.5) * mm});
            skSolve(sketch);
        }
        {
            var Q0;
            Q0=makeQuery(id+"F85.imprint","IMPRINT",FACE,{"disambiguationData":[TD([[makeQuery(id+"F85.imprint","IMPRINT",EDGE,{"derivedFrom":sQuery(id+"F85.wireOp",EDGE,"E45.bottom")}),-1.0]])]});
            extrude(context, id + "F86", {"entities" : qUnion([Q0]), "operationType" : NewBodyOperationType.ADD, "depth" : .5 * mm, "offsetDistance" : 25 * mm});
        }
        {
            var Q0;
            Q0=makeQuery(id+"F86.opExtrude","CAP_EDGE",EDGE,{"disambiguationData":[OSD([sQuery(id+"F85.wireOp",EDGE,"E45.top")])],"isStart":false});
            var Q1;
            Q1=makeQuery(id+"F86.opExtrude","CAP_EDGE",EDGE,{"disambiguationData":[OSD([sQuery(id+"F85.wireOp",EDGE,"E45.bottom")])],"isStart":false});
            chamfer(context, id + "F87", {"entities" : qUnion([Q0, Q1]), "chamferType" : ChamferType.TWO_OFFSETS, "width1" : 7 * mm, "oppositeDirection" : false, "width2" : .5 * mm, "tangentPropagation" : true});
        }
        {
            var Q0;
            Q0=makeQuery(id+"F1.opExtrude","SWEPT_FACE",FACE,{"disambiguationData":[OSD([sQuery(id+"F0.wireOp",EDGE,"E10.2.44")])]});
            var sketch = newSketch(context, id + "F88", { "sketchPlane" : qUnion([Q0])});
            skLineSegment(sketch, "E46.bottom", {"start": v(-55.75, 3.5) * mm, "end": v(-58.75, 3.5) * mm});
            skLineSegment(sketch, "E46.top", {"start": v(-55.75, 17.5) * mm, "end": v(-58.75, 17.5) * mm});
            skLineSegment(sketch, "E46.left", {"start": v(-55.75, 3.5) * mm, "end": v(-55.75, 17.5) * mm});
            skLineSegment(sketch, "E46.right", {"start": v(-58.75, 3.5) * mm, "end": v(-58.75, 17.5) * mm});
            skPoint(sketch, "E46.middle", {"position": v(-57.25, 10.5) * mm});
            skSolve(sketch);
        }
        {
            var Q0;
            Q0=makeQuery(id+"F88.imprint","IMPRINT",FACE,{"disambiguationData":[TD([[makeQuery(id+"F88.imprint","IMPRINT",EDGE,{"derivedFrom":sQuery(id+"F88.wireOp",EDGE,"E46.bottom")}),-1.0]])]});
            extrude(context, id + "F89", {"entities" : qUnion([Q0]), "operationType" : NewBodyOperationType.ADD, "depth" : .5 * mm, "offsetDistance" : 25 * mm});
        }
        {
            var Q0;
            Q0=makeQuery(id+"F89.opExtrude","CAP_EDGE",EDGE,{"disambiguationData":[OSD([sQuery(id+"F88.wireOp",EDGE,"E46.top")])],"isStart":false});
            var Q1;
            Q1=makeQuery(id+"F89.opExtrude","CAP_EDGE",EDGE,{"disambiguationData":[OSD([sQuery(id+"F88.wireOp",EDGE,"E46.bottom")])],"isStart":false});
            chamfer(context, id + "F90", {"entities" : qUnion([Q0, Q1]), "chamferType" : ChamferType.TWO_OFFSETS, "width1" : 7 * mm, "oppositeDirection" : false, "width2" : .5 * mm, "tangentPropagation" : true});
        }
        {
            var Q0;
            Q0=makeQuery(id+"F1.opExtrude","SWEPT_FACE",FACE,{"disambiguationData":[OSD([sQuery(id+"F0.wireOp",EDGE,"E10.2.40")])]});
            var sketch = newSketch(context, id + "F91", { "sketchPlane" : qUnion([Q0])});
            skLineSegment(sketch, "E47.bottom", {"start": v(-22.84, 3.5) * mm, "end": v(-25.84, 3.5) * mm});
            skLineSegment(sketch, "E47.top", {"start": v(-22.84, 17.5) * mm, "end": v(-25.84, 17.5) * mm});
            skLineSegment(sketch, "E47.left", {"start": v(-22.84, 3.5) * mm, "end": v(-22.84, 17.5) * mm});
            skLineSegment(sketch, "E47.right", {"start": v(-25.84, 3.5) * mm, "end": v(-25.84, 17.5) * mm});
            skPoint(sketch, "E47.middle", {"position": v(-24.34, 10.5) * mm});
            skLineSegment(sketch, "E48.bottom", {"start": v(-88.66, 3.5) * mm, "end": v(-91.66, 3.5) * mm});
            skLineSegment(sketch, "E48.top", {"start": v(-88.66, 17.5) * mm, "end": v(-91.66, 17.5) * mm});
            skLineSegment(sketch, "E48.left", {"start": v(-88.66, 3.5) * mm, "end": v(-88.66, 17.5) * mm});
            skLineSegment(sketch, "E48.right", {"start": v(-91.66, 3.5) * mm, "end": v(-91.66, 17.5) * mm});
            skPoint(sketch, "E48.middle", {"position": v(-90.16, 10.5) * mm});
            skSolve(sketch);
        }
        {
            var Q0;
            Q0=makeQuery(id+"F91.imprint","IMPRINT",FACE,{"disambiguationData":[TD([[makeQuery(id+"F91.imprint","IMPRINT",EDGE,{"derivedFrom":sQuery(id+"F91.wireOp",EDGE,"E48.bottom")}),-1.0]])]});
            var Q1;
            Q1=makeQuery(id+"F91.imprint","IMPRINT",FACE,{"disambiguationData":[TD([[makeQuery(id+"F91.imprint","IMPRINT",EDGE,{"derivedFrom":sQuery(id+"F91.wireOp",EDGE,"E47.bottom")}),-1.0]])]});
            extrude(context, id + "F92", {"entities" : qUnion([Q0, Q1]), "operationType" : NewBodyOperationType.ADD, "depth" : .5 * mm, "offsetDistance" : 25 * mm});
        }
        {
            var Q0;
            Q0=makeQuery(id+"F92.opExtrude","CAP_EDGE",EDGE,{"disambiguationData":[OSD([sQuery(id+"F91.wireOp",EDGE,"E48.top")])],"isStart":false});
            var Q1;
            Q1=makeQuery(id+"F92.opExtrude","CAP_EDGE",EDGE,{"disambiguationData":[OSD([sQuery(id+"F91.wireOp",EDGE,"E48.bottom")])],"isStart":false});
            var Q2;
            Q2=makeQuery(id+"F92.opExtrude","CAP_EDGE",EDGE,{"disambiguationData":[OSD([sQuery(id+"F91.wireOp",EDGE,"E47.top")])],"isStart":false});
            chamfer(context, id + "F93", {"entities" : qUnion([Q0, Q1, Q2]), "chamferType" : ChamferType.TWO_OFFSETS, "width1" : 7 * mm, "oppositeDirection" : false, "width2" : .5 * mm, "tangentPropagation" : true});
        }
        {
            var Q0;
            Q0=makeQuery(id+"F92.opExtrude","CAP_EDGE",EDGE,{"disambiguationData":[OSD([sQuery(id+"F91.wireOp",EDGE,"E47.bottom")])],"isStart":false});
            chamfer(context, id + "F94", {"entities" : qUnion([Q0]), "chamferType" : ChamferType.TWO_OFFSETS, "width1" : 7 * mm, "oppositeDirection" : true, "width2" : .5 * mm, "tangentPropagation" : true});
        }
        {
            var Q0;
            Q0=makeQuery(id+"F1.opExtrude","SWEPT_FACE",FACE,{"disambiguationData":[OSD([sQuery(id+"F0.wireOp",EDGE,"E10.2.42")])]});
            var sketch = newSketch(context, id + "F95", { "sketchPlane" : qUnion([Q0])});
            skLineSegment(sketch, "E49.bottom", {"start": v(-55.75, 3.5) * mm, "end": v(-58.75, 3.5) * mm});
            skLineSegment(sketch, "E49.top", {"start": v(-55.75, 17.5) * mm, "end": v(-58.75, 17.5) * mm});
            skLineSegment(sketch, "E49.left", {"start": v(-55.75, 3.5) * mm, "end": v(-55.75, 17.5) * mm});
            skLineSegment(sketch, "E49.right", {"start": v(-58.75, 3.5) * mm, "end": v(-58.75, 17.5) * mm});
            skPoint(sketch, "E49.middle", {"position": v(-57.25, 10.5) * mm});
            skSolve(sketch);
        }
        {
            var Q0;
            Q0=makeQuery(id+"F95.imprint","IMPRINT",FACE,{"disambiguationData":[TD([[makeQuery(id+"F95.imprint","IMPRINT",EDGE,{"derivedFrom":sQuery(id+"F95.wireOp",EDGE,"E49.bottom")}),-1.0]])]});
            extrude(context, id + "F96", {"entities" : qUnion([Q0]), "operationType" : NewBodyOperationType.ADD, "depth" : .5 * mm, "offsetDistance" : 25 * mm});
        }
        {
            var Q0;
            Q0=makeQuery(id+"F96.opExtrude","CAP_EDGE",EDGE,{"disambiguationData":[OSD([sQuery(id+"F95.wireOp",EDGE,"E49.top")])],"isStart":false});
            var Q1;
            Q1=makeQuery(id+"F96.opExtrude","CAP_EDGE",EDGE,{"disambiguationData":[OSD([sQuery(id+"F95.wireOp",EDGE,"E49.bottom")])],"isStart":false});
            chamfer(context, id + "F97", {"entities" : qUnion([Q0, Q1]), "chamferType" : ChamferType.TWO_OFFSETS, "width1" : 7 * mm, "oppositeDirection" : false, "width2" : .5 * mm, "tangentPropagation" : true});
        }
        {
            var Q0;
            Q0=makeQuery(id+"F1.opExtrude","SWEPT_FACE",FACE,{"disambiguationData":[OSD([sQuery(id+"F0.wireOp",EDGE,"E10.2.52")])]});
            var sketch = newSketch(context, id + "F98", { "sketchPlane" : qUnion([Q0])});
            skLineSegment(sketch, "E50.bottom", {"start": v(-22.84, 3.5) * mm, "end": v(-25.84, 3.5) * mm});
            skLineSegment(sketch, "E50.top", {"start": v(-22.84, 17.5) * mm, "end": v(-25.84, 17.5) * mm});
            skLineSegment(sketch, "E50.left", {"start": v(-22.84, 3.5) * mm, "end": v(-22.84, 17.5) * mm});
            skLineSegment(sketch, "E50.right", {"start": v(-25.84, 3.5) * mm, "end": v(-25.84, 17.5) * mm});
            skPoint(sketch, "E50.middle", {"position": v(-24.34, 10.5) * mm});
            skLineSegment(sketch, "E51.bottom", {"start": v(-88.66, 3.5) * mm, "end": v(-91.66, 3.5) * mm});
            skLineSegment(sketch, "E51.top", {"start": v(-88.66, 17.5) * mm, "end": v(-91.66, 17.5) * mm});
            skLineSegment(sketch, "E51.left", {"start": v(-88.66, 3.5) * mm, "end": v(-88.66, 17.5) * mm});
            skLineSegment(sketch, "E51.right", {"start": v(-91.66, 3.5) * mm, "end": v(-91.66, 17.5) * mm});
            skPoint(sketch, "E51.middle", {"position": v(-90.16, 10.5) * mm});
            skSolve(sketch);
        }
        {
            var Q0;
            Q0=makeQuery(id+"F98.imprint","IMPRINT",FACE,{"disambiguationData":[TD([[makeQuery(id+"F98.imprint","IMPRINT",EDGE,{"derivedFrom":sQuery(id+"F98.wireOp",EDGE,"E51.bottom")}),-1.0]])]});
            var Q1;
            Q1=makeQuery(id+"F98.imprint","IMPRINT",FACE,{"disambiguationData":[TD([[makeQuery(id+"F98.imprint","IMPRINT",EDGE,{"derivedFrom":sQuery(id+"F98.wireOp",EDGE,"E50.bottom")}),-1.0]])]});
            extrude(context, id + "F99", {"entities" : qUnion([Q0, Q1]), "operationType" : NewBodyOperationType.ADD, "depth" : .5 * mm, "offsetDistance" : 25 * mm});
        }
        {
            var Q0;
            Q0=makeQuery(id+"F99.opExtrude","CAP_EDGE",EDGE,{"disambiguationData":[OSD([sQuery(id+"F98.wireOp",EDGE,"E51.top")])],"isStart":false});
            var Q1;
            Q1=makeQuery(id+"F99.opExtrude","CAP_EDGE",EDGE,{"disambiguationData":[OSD([sQuery(id+"F98.wireOp",EDGE,"E51.bottom")])],"isStart":false});
            var Q2;
            Q2=makeQuery(id+"F99.opExtrude","CAP_EDGE",EDGE,{"disambiguationData":[OSD([sQuery(id+"F98.wireOp",EDGE,"E50.top")])],"isStart":false});
            chamfer(context, id + "F100", {"entities" : qUnion([Q0, Q1, Q2]), "chamferType" : ChamferType.TWO_OFFSETS, "width1" : 7 * mm, "oppositeDirection" : false, "width2" : .5 * mm, "tangentPropagation" : true});
        }
        {
            var Q0;
            Q0=makeQuery(id+"F99.opExtrude","CAP_EDGE",EDGE,{"disambiguationData":[OSD([sQuery(id+"F98.wireOp",EDGE,"E50.bottom")])],"isStart":false});
            chamfer(context, id + "F101", {"entities" : qUnion([Q0]), "chamferType" : ChamferType.TWO_OFFSETS, "width1" : 7 * mm, "oppositeDirection" : true, "width2" : .5 * mm, "tangentPropagation" : true});
        }
        {
            var Q0;
            Q0=makeQuery(id+"F1.opExtrude","SWEPT_FACE",FACE,{"disambiguationData":[OSD([sQuery(id+"F0.wireOp",EDGE,"E10.2.49")])]});
            var sketch = newSketch(context, id + "F102", { "sketchPlane" : qUnion([Q0])});
            skLineSegment(sketch, "E52.bottom", {"start": v(-55.75, 3.5) * mm, "end": v(-58.75, 3.5) * mm});
            skLineSegment(sketch, "E52.top", {"start": v(-55.75, 17.5) * mm, "end": v(-58.75, 17.5) * mm});
            skLineSegment(sketch, "E52.left", {"start": v(-55.75, 3.5) * mm, "end": v(-55.75, 17.5) * mm});
            skLineSegment(sketch, "E52.right", {"start": v(-58.75, 3.5) * mm, "end": v(-58.75, 17.5) * mm});
            skPoint(sketch, "E52.middle", {"position": v(-57.25, 10.5) * mm});
            skSolve(sketch);
        }
        {
            var Q0;
            Q0=makeQuery(id+"F102.imprint","IMPRINT",FACE,{"disambiguationData":[TD([[makeQuery(id+"F102.imprint","IMPRINT",EDGE,{"derivedFrom":sQuery(id+"F102.wireOp",EDGE,"E52.bottom")}),-1.0]])]});
            extrude(context, id + "F103", {"entities" : qUnion([Q0]), "operationType" : NewBodyOperationType.ADD, "depth" : .5 * mm, "offsetDistance" : 25 * mm});
        }
        {
            var Q0;
            Q0=makeQuery(id+"F103.opExtrude","CAP_EDGE",EDGE,{"disambiguationData":[OSD([sQuery(id+"F102.wireOp",EDGE,"E52.top")])],"isStart":false});
            var Q1;
            Q1=makeQuery(id+"F103.opExtrude","CAP_EDGE",EDGE,{"disambiguationData":[OSD([sQuery(id+"F102.wireOp",EDGE,"E52.bottom")])],"isStart":false});
            chamfer(context, id + "F104", {"entities" : qUnion([Q0, Q1]), "chamferType" : ChamferType.TWO_OFFSETS, "width1" : 7 * mm, "oppositeDirection" : false, "width2" : .5 * mm, "tangentPropagation" : true});
        }
        {
            var Q0;
            Q0=makeQuery(id+"F1.opExtrude","SWEPT_FACE",FACE,{"disambiguationData":[OSD([sQuery(id+"F0.wireOp",EDGE,"E10.2.43")])]});
            var sketch = newSketch(context, id + "F105", { "sketchPlane" : qUnion([Q0])});
            skLineSegment(sketch, "E53.bottom", {"start": v(-55.75, 3.5) * mm, "end": v(-58.75, 3.5) * mm});
            skLineSegment(sketch, "E53.top", {"start": v(-55.75, 17.5) * mm, "end": v(-58.75, 17.5) * mm});
            skLineSegment(sketch, "E53.left", {"start": v(-55.75, 3.5) * mm, "end": v(-55.75, 17.5) * mm});
            skLineSegment(sketch, "E53.right", {"start": v(-58.75, 3.5) * mm, "end": v(-58.75, 17.5) * mm});
            skPoint(sketch, "E53.middle", {"position": v(-57.25, 10.5) * mm});
            skSolve(sketch);
        }
        {
            var Q0;
            Q0=makeQuery(id+"F105.imprint","IMPRINT",FACE,{"disambiguationData":[TD([[makeQuery(id+"F105.imprint","IMPRINT",EDGE,{"derivedFrom":sQuery(id+"F105.wireOp",EDGE,"E53.bottom")}),-1.0]])]});
            extrude(context, id + "F106", {"entities" : qUnion([Q0]), "operationType" : NewBodyOperationType.ADD, "depth" : .5 * mm, "offsetDistance" : 25 * mm});
        }
        {
            var Q0;
            Q0=makeQuery(id+"F106.opExtrude","CAP_EDGE",EDGE,{"disambiguationData":[OSD([sQuery(id+"F105.wireOp",EDGE,"E53.top")])],"isStart":false});
            var Q1;
            Q1=makeQuery(id+"F106.opExtrude","CAP_EDGE",EDGE,{"disambiguationData":[OSD([sQuery(id+"F105.wireOp",EDGE,"E53.bottom")])],"isStart":false});
            chamfer(context, id + "F107", {"entities" : qUnion([Q0, Q1]), "chamferType" : ChamferType.TWO_OFFSETS, "width1" : 7 * mm, "oppositeDirection" : false, "width2" : .5 * mm, "tangentPropagation" : true});
        }
        {
            var Q0;
            Q0=makeQuery(id+"F1.opExtrude","SWEPT_FACE",FACE,{"disambiguationData":[OSD([sQuery(id+"F0.wireOp",EDGE,"E10.2.33")])]});
            var sketch = newSketch(context, id + "F108", { "sketchPlane" : qUnion([Q0])});
            skLineSegment(sketch, "E54.bottom", {"start": v(-22.84, 3.5) * mm, "end": v(-25.84, 3.5) * mm});
            skLineSegment(sketch, "E54.top", {"start": v(-22.84, 17.5) * mm, "end": v(-25.84, 17.5) * mm});
            skLineSegment(sketch, "E54.left", {"start": v(-22.84, 3.5) * mm, "end": v(-22.84, 17.5) * mm});
            skLineSegment(sketch, "E54.right", {"start": v(-25.84, 3.5) * mm, "end": v(-25.84, 17.5) * mm});
            skPoint(sketch, "E54.middle", {"position": v(-24.34, 10.5) * mm});
            skLineSegment(sketch, "E55.bottom", {"start": v(-88.66, 3.5) * mm, "end": v(-91.66, 3.5) * mm});
            skLineSegment(sketch, "E55.top", {"start": v(-88.66, 17.5) * mm, "end": v(-91.66, 17.5) * mm});
            skLineSegment(sketch, "E55.left", {"start": v(-88.66, 3.5) * mm, "end": v(-88.66, 17.5) * mm});
            skLineSegment(sketch, "E55.right", {"start": v(-91.66, 3.5) * mm, "end": v(-91.66, 17.5) * mm});
            skPoint(sketch, "E55.middle", {"position": v(-90.16, 10.5) * mm});
            skSolve(sketch);
        }
        {
            var Q0;
            Q0=makeQuery(id+"F108.imprint","IMPRINT",FACE,{"disambiguationData":[TD([[makeQuery(id+"F108.imprint","IMPRINT",EDGE,{"derivedFrom":sQuery(id+"F108.wireOp",EDGE,"E55.bottom")}),-1.0]])]});
            var Q1;
            Q1=makeQuery(id+"F108.imprint","IMPRINT",FACE,{"disambiguationData":[TD([[makeQuery(id+"F108.imprint","IMPRINT",EDGE,{"derivedFrom":sQuery(id+"F108.wireOp",EDGE,"E54.bottom")}),-1.0]])]});
            extrude(context, id + "F109", {"entities" : qUnion([Q0, Q1]), "operationType" : NewBodyOperationType.ADD, "depth" : .5 * mm, "offsetDistance" : 25 * mm});
        }
        {
            var Q0;
            Q0=makeQuery(id+"F109.opExtrude","CAP_EDGE",EDGE,{"disambiguationData":[OSD([sQuery(id+"F108.wireOp",EDGE,"E55.top")])],"isStart":false});
            var Q1;
            Q1=makeQuery(id+"F109.opExtrude","CAP_EDGE",EDGE,{"disambiguationData":[OSD([sQuery(id+"F108.wireOp",EDGE,"E55.bottom")])],"isStart":false});
            var Q2;
            Q2=makeQuery(id+"F109.opExtrude","CAP_EDGE",EDGE,{"disambiguationData":[OSD([sQuery(id+"F108.wireOp",EDGE,"E54.top")])],"isStart":false});
            chamfer(context, id + "F110", {"entities" : qUnion([Q0, Q1, Q2]), "chamferType" : ChamferType.TWO_OFFSETS, "width1" : 7 * mm, "oppositeDirection" : false, "width2" : .5 * mm, "tangentPropagation" : true});
        }
        {
            var Q0;
            Q0=makeQuery(id+"F109.opExtrude","CAP_EDGE",EDGE,{"disambiguationData":[OSD([sQuery(id+"F108.wireOp",EDGE,"E54.bottom")])],"isStart":false});
            chamfer(context, id + "F111", {"entities" : qUnion([Q0]), "chamferType" : ChamferType.TWO_OFFSETS, "width1" : 7 * mm, "oppositeDirection" : true, "width2" : .5 * mm, "tangentPropagation" : true});
        }
        {
            var Q0;
            Q0=makeQuery(id+"F1.opExtrude","SWEPT_FACE",FACE,{"disambiguationData":[OSD([sQuery(id+"F0.wireOp",EDGE,"E10.2.46")])]});
            var sketch = newSketch(context, id + "F112", { "sketchPlane" : qUnion([Q0])});
            skLineSegment(sketch, "E56.bottom", {"start": v(-55.75, 3.5) * mm, "end": v(-58.75, 3.5) * mm});
            skLineSegment(sketch, "E56.top", {"start": v(-55.75, 17.5) * mm, "end": v(-58.75, 17.5) * mm});
            skLineSegment(sketch, "E56.left", {"start": v(-55.75, 3.5) * mm, "end": v(-55.75, 17.5) * mm});
            skLineSegment(sketch, "E56.right", {"start": v(-58.75, 3.5) * mm, "end": v(-58.75, 17.5) * mm});
            skPoint(sketch, "E56.middle", {"position": v(-57.25, 10.5) * mm});
            skSolve(sketch);
        }
        {
            var Q0;
            Q0=makeQuery(id+"F112.imprint","IMPRINT",FACE,{"disambiguationData":[TD([[makeQuery(id+"F112.imprint","IMPRINT",EDGE,{"derivedFrom":sQuery(id+"F112.wireOp",EDGE,"E56.bottom")}),-1.0]])]});
            extrude(context, id + "F113", {"entities" : qUnion([Q0]), "operationType" : NewBodyOperationType.ADD, "depth" : .5 * mm, "offsetDistance" : 25 * mm});
        }
        {
            var Q0;
            Q0=makeQuery(id+"F113.opExtrude","CAP_EDGE",EDGE,{"disambiguationData":[OSD([sQuery(id+"F112.wireOp",EDGE,"E56.top")])],"isStart":false});
            var Q1;
            Q1=makeQuery(id+"F113.opExtrude","CAP_EDGE",EDGE,{"disambiguationData":[OSD([sQuery(id+"F112.wireOp",EDGE,"E56.bottom")])],"isStart":false});
            chamfer(context, id + "F114", {"entities" : qUnion([Q0, Q1]), "chamferType" : ChamferType.TWO_OFFSETS, "width1" : 7 * mm, "oppositeDirection" : false, "width2" : .5 * mm, "tangentPropagation" : true});
        }
        {
            var Q0;
            Q0=makeQuery(id+"F1.opExtrude","SWEPT_FACE",FACE,{"disambiguationData":[OSD([sQuery(id+"F0.wireOp",EDGE,"E10.2.28")])]});
            var sketch = newSketch(context, id + "F115", { "sketchPlane" : qUnion([Q0])});
            skLineSegment(sketch, "E57.bottom", {"start": v(-22.84, 3.5) * mm, "end": v(-25.84, 3.5) * mm});
            skLineSegment(sketch, "E57.top", {"start": v(-22.84, 17.5) * mm, "end": v(-25.84, 17.5) * mm});
            skLineSegment(sketch, "E57.left", {"start": v(-22.84, 3.5) * mm, "end": v(-22.84, 17.5) * mm});
            skLineSegment(sketch, "E57.right", {"start": v(-25.84, 3.5) * mm, "end": v(-25.84, 17.5) * mm});
            skPoint(sketch, "E57.middle", {"position": v(-24.34, 10.5) * mm});
            skLineSegment(sketch, "E58.bottom", {"start": v(-88.66, 3.5) * mm, "end": v(-91.66, 3.5) * mm});
            skLineSegment(sketch, "E58.top", {"start": v(-88.66, 17.5) * mm, "end": v(-91.66, 17.5) * mm});
            skLineSegment(sketch, "E58.left", {"start": v(-88.66, 3.5) * mm, "end": v(-88.66, 17.5) * mm});
            skLineSegment(sketch, "E58.right", {"start": v(-91.66, 3.5) * mm, "end": v(-91.66, 17.5) * mm});
            skPoint(sketch, "E58.middle", {"position": v(-90.16, 10.5) * mm});
            skSolve(sketch);
        }
        {
            var Q0;
            Q0=makeQuery(id+"F115.imprint","IMPRINT",FACE,{"disambiguationData":[TD([[makeQuery(id+"F115.imprint","IMPRINT",EDGE,{"derivedFrom":sQuery(id+"F115.wireOp",EDGE,"E58.bottom")}),-1.0]])]});
            var Q1;
            Q1=makeQuery(id+"F115.imprint","IMPRINT",FACE,{"disambiguationData":[TD([[makeQuery(id+"F115.imprint","IMPRINT",EDGE,{"derivedFrom":sQuery(id+"F115.wireOp",EDGE,"E57.bottom")}),-1.0]])]});
            extrude(context, id + "F116", {"entities" : qUnion([Q0, Q1]), "operationType" : NewBodyOperationType.ADD, "depth" : .5 * mm, "offsetDistance" : 25 * mm});
        }
        {
            var Q0;
            Q0=makeQuery(id+"F116.opExtrude","CAP_EDGE",EDGE,{"disambiguationData":[OSD([sQuery(id+"F115.wireOp",EDGE,"E58.top")])],"isStart":false});
            var Q1;
            Q1=makeQuery(id+"F116.opExtrude","CAP_EDGE",EDGE,{"disambiguationData":[OSD([sQuery(id+"F115.wireOp",EDGE,"E58.bottom")])],"isStart":false});
            var Q2;
            Q2=makeQuery(id+"F116.opExtrude","CAP_EDGE",EDGE,{"disambiguationData":[OSD([sQuery(id+"F115.wireOp",EDGE,"E57.top")])],"isStart":false});
            chamfer(context, id + "F117", {"entities" : qUnion([Q0, Q1, Q2]), "chamferType" : ChamferType.TWO_OFFSETS, "width1" : 7 * mm, "oppositeDirection" : false, "width2" : .5 * mm, "tangentPropagation" : true});
        }
        {
            var Q0;
            Q0=makeQuery(id+"F116.opExtrude","CAP_EDGE",EDGE,{"disambiguationData":[OSD([sQuery(id+"F115.wireOp",EDGE,"E57.bottom")])],"isStart":false});
            chamfer(context, id + "F118", {"entities" : qUnion([Q0]), "chamferType" : ChamferType.TWO_OFFSETS, "width1" : 7 * mm, "oppositeDirection" : true, "width2" : .5 * mm, "tangentPropagation" : true});
        }
        {
            var Q0;
            Q0=makeQuery(id+"F1.opExtrude","SWEPT_FACE",FACE,{"disambiguationData":[OSD([sQuery(id+"F0.wireOp",EDGE,"E10.2.47")])]});
            var sketch = newSketch(context, id + "F119", { "sketchPlane" : qUnion([Q0])});
            skLineSegment(sketch, "E59.bottom", {"start": v(-55.75, 3.5) * mm, "end": v(-58.75, 3.5) * mm});
            skLineSegment(sketch, "E59.top", {"start": v(-55.75, 17.5) * mm, "end": v(-58.75, 17.5) * mm});
            skLineSegment(sketch, "E59.left", {"start": v(-55.75, 3.5) * mm, "end": v(-55.75, 17.5) * mm});
            skLineSegment(sketch, "E59.right", {"start": v(-58.75, 3.5) * mm, "end": v(-58.75, 17.5) * mm});
            skPoint(sketch, "E59.middle", {"position": v(-57.25, 10.5) * mm});
            skSolve(sketch);
        }
        {
            var Q0;
            Q0=makeQuery(id+"F119.imprint","IMPRINT",FACE,{"disambiguationData":[TD([[makeQuery(id+"F119.imprint","IMPRINT",EDGE,{"derivedFrom":sQuery(id+"F119.wireOp",EDGE,"E59.bottom")}),-1.0]])]});
            extrude(context, id + "F120", {"entities" : qUnion([Q0]), "operationType" : NewBodyOperationType.ADD, "depth" : .5 * mm, "offsetDistance" : 25 * mm});
        }
        {
            var Q0;
            Q0=makeQuery(id+"F120.opExtrude","CAP_EDGE",EDGE,{"disambiguationData":[OSD([sQuery(id+"F119.wireOp",EDGE,"E59.top")])],"isStart":false});
            var Q1;
            Q1=makeQuery(id+"F120.opExtrude","CAP_EDGE",EDGE,{"disambiguationData":[OSD([sQuery(id+"F119.wireOp",EDGE,"E59.bottom")])],"isStart":false});
            chamfer(context, id + "F121", {"entities" : qUnion([Q0, Q1]), "chamferType" : ChamferType.TWO_OFFSETS, "width1" : 7 * mm, "oppositeDirection" : false, "width2" : .5 * mm, "tangentPropagation" : true});
        }
        {
            var Q0;
            Q0=makeQuery(id+"F1.opExtrude","SWEPT_FACE",FACE,{"disambiguationData":[OSD([sQuery(id+"F0.wireOp",EDGE,"E10.1.48")])]});
            var sketch = newSketch(context, id + "F122", { "sketchPlane" : qUnion([Q0])});
            skLineSegment(sketch, "E60.bottom", {"start": v(116, 3.5) * mm, "end": v(113, 3.5) * mm});
            skLineSegment(sketch, "E60.top", {"start": v(116, 17.5) * mm, "end": v(113, 17.5) * mm});
            skLineSegment(sketch, "E60.left", {"start": v(116, 3.5) * mm, "end": v(116, 17.5) * mm});
            skLineSegment(sketch, "E60.right", {"start": v(113, 3.5) * mm, "end": v(113, 17.5) * mm});
            skPoint(sketch, "E60.middle", {"position": v(114.5, 10.5) * mm});
            skSolve(sketch);
        }
        {
            var Q0;
            Q0=makeQuery(id+"F122.imprint","IMPRINT",FACE,{"disambiguationData":[TD([[makeQuery(id+"F122.imprint","IMPRINT",EDGE,{"derivedFrom":sQuery(id+"F122.wireOp",EDGE,"E60.bottom")}),-1.0]])]});
            extrude(context, id + "F123", {"entities" : qUnion([Q0]), "operationType" : NewBodyOperationType.ADD, "depth" : .5 * mm, "offsetDistance" : 25 * mm});
        }
        {
            var Q0;
            Q0=makeQuery(id+"F123.opExtrude","CAP_EDGE",EDGE,{"disambiguationData":[OSD([sQuery(id+"F122.wireOp",EDGE,"E60.top")])],"isStart":false});
            var Q1;
            Q1=makeQuery(id+"F123.opExtrude","CAP_EDGE",EDGE,{"disambiguationData":[OSD([sQuery(id+"F122.wireOp",EDGE,"E60.bottom")])],"isStart":false});
            chamfer(context, id + "F124", {"entities" : qUnion([Q0, Q1]), "chamferType" : ChamferType.TWO_OFFSETS, "width1" : 7 * mm, "oppositeDirection" : false, "width2" : .5 * mm, "tangentPropagation" : true});
        }
        {
            var Q0;
            Q0=makeQuery(id+"F1.opExtrude","SWEPT_FACE",FACE,{"disambiguationData":[OSD([sQuery(id+"F0.wireOp",EDGE,"E10.1.19")])]});
            var sketch = newSketch(context, id + "F125", { "sketchPlane" : qUnion([Q0])});
            skLineSegment(sketch, "E61.bottom", {"start": v(148.9, 3.5) * mm, "end": v(145.9, 3.5) * mm});
            skLineSegment(sketch, "E61.top", {"start": v(148.9, 17.5) * mm, "end": v(145.9, 17.5) * mm});
            skLineSegment(sketch, "E61.left", {"start": v(148.9, 3.5) * mm, "end": v(148.9, 17.5) * mm});
            skLineSegment(sketch, "E61.right", {"start": v(145.9, 3.5) * mm, "end": v(145.9, 17.5) * mm});
            skPoint(sketch, "E61.middle", {"position": v(147.4, 10.5) * mm});
            skLineSegment(sketch, "E62.bottom", {"start": v(83.1, 3.5) * mm, "end": v(80.1, 3.5) * mm});
            skLineSegment(sketch, "E62.top", {"start": v(83.1, 17.5) * mm, "end": v(80.1, 17.5) * mm});
            skLineSegment(sketch, "E62.left", {"start": v(83.1, 3.5) * mm, "end": v(83.1, 17.5) * mm});
            skLineSegment(sketch, "E62.right", {"start": v(80.1, 3.5) * mm, "end": v(80.1, 17.5) * mm});
            skPoint(sketch, "E62.middle", {"position": v(81.6, 10.5) * mm});
            skSolve(sketch);
        }
        {
            var Q0;
            Q0=makeQuery(id+"F125.imprint","IMPRINT",FACE,{"disambiguationData":[TD([[makeQuery(id+"F125.imprint","IMPRINT",EDGE,{"derivedFrom":sQuery(id+"F125.wireOp",EDGE,"E62.bottom")}),-1.0]])]});
            var Q1;
            Q1=makeQuery(id+"F125.imprint","IMPRINT",FACE,{"disambiguationData":[TD([[makeQuery(id+"F125.imprint","IMPRINT",EDGE,{"derivedFrom":sQuery(id+"F125.wireOp",EDGE,"E61.bottom")}),-1.0]])]});
            extrude(context, id + "F126", {"entities" : qUnion([Q0, Q1]), "operationType" : NewBodyOperationType.ADD, "depth" : .5 * mm, "offsetDistance" : 25 * mm});
        }
        {
            var Q0;
            Q0=makeQuery(id+"F126.opExtrude","CAP_EDGE",EDGE,{"disambiguationData":[OSD([sQuery(id+"F125.wireOp",EDGE,"E62.top")])],"isStart":false});
            var Q1;
            Q1=makeQuery(id+"F126.opExtrude","CAP_EDGE",EDGE,{"disambiguationData":[OSD([sQuery(id+"F125.wireOp",EDGE,"E62.bottom")])],"isStart":false});
            var Q2;
            Q2=makeQuery(id+"F126.opExtrude","CAP_EDGE",EDGE,{"disambiguationData":[OSD([sQuery(id+"F125.wireOp",EDGE,"E61.top")])],"isStart":false});
            chamfer(context, id + "F127", {"entities" : qUnion([Q0, Q1, Q2]), "chamferType" : ChamferType.TWO_OFFSETS, "width1" : 7 * mm, "oppositeDirection" : false, "width2" : .5 * mm, "tangentPropagation" : true});
        }
        {
            var Q0;
            Q0=makeQuery(id+"F126.opExtrude","CAP_EDGE",EDGE,{"disambiguationData":[OSD([sQuery(id+"F125.wireOp",EDGE,"E61.bottom")])],"isStart":false});
            chamfer(context, id + "F128", {"entities" : qUnion([Q0]), "chamferType" : ChamferType.TWO_OFFSETS, "width1" : 7 * mm, "oppositeDirection" : true, "width2" : .5 * mm, "tangentPropagation" : true});
        }
        {
            var Q0;
            Q0=makeQuery(id+"F1.opExtrude","SWEPT_FACE",FACE,{"disambiguationData":[OSD([sQuery(id+"F0.wireOp",EDGE,"E10.1.59")])]});
            var sketch = newSketch(context, id + "F129", { "sketchPlane" : qUnion([Q0])});
            skLineSegment(sketch, "E63.bottom", {"start": v(116, 3.5) * mm, "end": v(113, 3.5) * mm});
            skLineSegment(sketch, "E63.top", {"start": v(116, 17.5) * mm, "end": v(113, 17.5) * mm});
            skLineSegment(sketch, "E63.left", {"start": v(116, 3.5) * mm, "end": v(116, 17.5) * mm});
            skLineSegment(sketch, "E63.right", {"start": v(113, 3.5) * mm, "end": v(113, 17.5) * mm});
            skPoint(sketch, "E63.middle", {"position": v(114.5, 10.5) * mm});
            skSolve(sketch);
        }
        {
            var Q0;
            Q0=makeQuery(id+"F129.imprint","IMPRINT",FACE,{"disambiguationData":[TD([[makeQuery(id+"F129.imprint","IMPRINT",EDGE,{"derivedFrom":sQuery(id+"F129.wireOp",EDGE,"E63.bottom")}),-1.0]])]});
            extrude(context, id + "F130", {"entities" : qUnion([Q0]), "operationType" : NewBodyOperationType.ADD, "depth" : .5 * mm, "offsetDistance" : 25 * mm});
        }
        {
            var Q0;
            Q0=makeQuery(id+"F130.opExtrude","CAP_EDGE",EDGE,{"disambiguationData":[OSD([sQuery(id+"F129.wireOp",EDGE,"E63.top")])],"isStart":false});
            var Q1;
            Q1=makeQuery(id+"F130.opExtrude","CAP_EDGE",EDGE,{"disambiguationData":[OSD([sQuery(id+"F129.wireOp",EDGE,"E63.bottom")])],"isStart":false});
            chamfer(context, id + "F131", {"entities" : qUnion([Q0, Q1]), "chamferType" : ChamferType.TWO_OFFSETS, "width1" : 7 * mm, "oppositeDirection" : false, "width2" : .5 * mm, "tangentPropagation" : true});
        }
        {
            var Q0;
            Q0=makeQuery(id+"F1.opExtrude","SWEPT_FACE",FACE,{"disambiguationData":[OSD([sQuery(id+"F0.wireOp",EDGE,"E10.1.20")])]});
            var sketch = newSketch(context, id + "F132", { "sketchPlane" : qUnion([Q0])});
            skLineSegment(sketch, "E64.bottom", {"start": v(148.9, 3.5) * mm, "end": v(145.9, 3.5) * mm});
            skLineSegment(sketch, "E64.top", {"start": v(148.9, 17.5) * mm, "end": v(145.9, 17.5) * mm});
            skLineSegment(sketch, "E64.left", {"start": v(148.9, 3.5) * mm, "end": v(148.9, 17.5) * mm});
            skLineSegment(sketch, "E64.right", {"start": v(145.9, 3.5) * mm, "end": v(145.9, 17.5) * mm});
            skPoint(sketch, "E64.middle", {"position": v(147.4, 10.5) * mm});
            skLineSegment(sketch, "E65.bottom", {"start": v(83.1, 3.5) * mm, "end": v(80.1, 3.5) * mm});
            skLineSegment(sketch, "E65.top", {"start": v(83.1, 17.5) * mm, "end": v(80.1, 17.5) * mm});
            skLineSegment(sketch, "E65.left", {"start": v(83.1, 3.5) * mm, "end": v(83.1, 17.5) * mm});
            skLineSegment(sketch, "E65.right", {"start": v(80.1, 3.5) * mm, "end": v(80.1, 17.5) * mm});
            skPoint(sketch, "E65.middle", {"position": v(81.6, 10.5) * mm});
            skSolve(sketch);
        }
        {
            var Q0;
            Q0=makeQuery(id+"F132.imprint","IMPRINT",FACE,{"disambiguationData":[TD([[makeQuery(id+"F132.imprint","IMPRINT",EDGE,{"derivedFrom":sQuery(id+"F132.wireOp",EDGE,"E65.bottom")}),-1.0]])]});
            var Q1;
            Q1=makeQuery(id+"F132.imprint","IMPRINT",FACE,{"disambiguationData":[TD([[makeQuery(id+"F132.imprint","IMPRINT",EDGE,{"derivedFrom":sQuery(id+"F132.wireOp",EDGE,"E64.bottom")}),-1.0]])]});
            extrude(context, id + "F133", {"entities" : qUnion([Q0, Q1]), "operationType" : NewBodyOperationType.ADD, "depth" : .5 * mm, "offsetDistance" : 25 * mm});
        }
        {
            var Q0;
            Q0=makeQuery(id+"F133.opExtrude","CAP_EDGE",EDGE,{"disambiguationData":[OSD([sQuery(id+"F132.wireOp",EDGE,"E65.top")])],"isStart":false});
            var Q1;
            Q1=makeQuery(id+"F133.opExtrude","CAP_EDGE",EDGE,{"disambiguationData":[OSD([sQuery(id+"F132.wireOp",EDGE,"E65.bottom")])],"isStart":false});
            var Q2;
            Q2=makeQuery(id+"F133.opExtrude","CAP_EDGE",EDGE,{"disambiguationData":[OSD([sQuery(id+"F132.wireOp",EDGE,"E64.top")])],"isStart":false});
            chamfer(context, id + "F134", {"entities" : qUnion([Q0, Q1, Q2]), "chamferType" : ChamferType.TWO_OFFSETS, "width1" : 7 * mm, "oppositeDirection" : false, "width2" : .5 * mm, "tangentPropagation" : true});
        }
        {
            var Q0;
            Q0=makeQuery(id+"F133.opExtrude","CAP_EDGE",EDGE,{"disambiguationData":[OSD([sQuery(id+"F132.wireOp",EDGE,"E64.bottom")])],"isStart":false});
            chamfer(context, id + "F135", {"entities" : qUnion([Q0]), "chamferType" : ChamferType.TWO_OFFSETS, "width1" : 7 * mm, "oppositeDirection" : true, "width2" : .5 * mm, "tangentPropagation" : true});
        }
        {
            var Q0;
            Q0=makeQuery(id+"F1.opExtrude","SWEPT_FACE",FACE,{"disambiguationData":[OSD([sQuery(id+"F0.wireOp",EDGE,"E10.1.45")])]});
            var sketch = newSketch(context, id + "F136", { "sketchPlane" : qUnion([Q0])});
            skLineSegment(sketch, "E66.bottom", {"start": v(116, 3.5) * mm, "end": v(113, 3.5) * mm});
            skLineSegment(sketch, "E66.top", {"start": v(116, 17.5) * mm, "end": v(113, 17.5) * mm});
            skLineSegment(sketch, "E66.left", {"start": v(116, 3.5) * mm, "end": v(116, 17.5) * mm});
            skLineSegment(sketch, "E66.right", {"start": v(113, 3.5) * mm, "end": v(113, 17.5) * mm});
            skPoint(sketch, "E66.middle", {"position": v(114.5, 10.5) * mm});
            skSolve(sketch);
        }
        {
            var Q0;
            Q0=makeQuery(id+"F136.imprint","IMPRINT",FACE,{"disambiguationData":[TD([[makeQuery(id+"F136.imprint","IMPRINT",EDGE,{"derivedFrom":sQuery(id+"F136.wireOp",EDGE,"E66.bottom")}),-1.0]])]});
            extrude(context, id + "F137", {"entities" : qUnion([Q0]), "operationType" : NewBodyOperationType.ADD, "depth" : .5 * mm, "offsetDistance" : 25 * mm});
        }
        {
            var Q0;
            Q0=makeQuery(id+"F137.opExtrude","CAP_EDGE",EDGE,{"disambiguationData":[OSD([sQuery(id+"F136.wireOp",EDGE,"E66.top")])],"isStart":false});
            var Q1;
            Q1=makeQuery(id+"F137.opExtrude","CAP_EDGE",EDGE,{"disambiguationData":[OSD([sQuery(id+"F136.wireOp",EDGE,"E66.bottom")])],"isStart":false});
            chamfer(context, id + "F138", {"entities" : qUnion([Q0, Q1]), "chamferType" : ChamferType.TWO_OFFSETS, "width1" : 7 * mm, "oppositeDirection" : false, "width2" : .5 * mm, "tangentPropagation" : true});
        }
        {
            var Q0;
            Q0=makeQuery(id+"F1.opExtrude","SWEPT_FACE",FACE,{"disambiguationData":[OSD([sQuery(id+"F0.wireOp",EDGE,"E2.0")])]});
            var sketch = newSketch(context, id + "F139", { "sketchPlane" : qUnion([Q0])});
            skLineSegment(sketch, "E67.bottom", {"start": v(-55.75, 3.5) * mm, "end": v(-58.75, 3.5) * mm});
            skLineSegment(sketch, "E67.top", {"start": v(-55.75, 17.5) * mm, "end": v(-58.75, 17.5) * mm});
            skLineSegment(sketch, "E67.left", {"start": v(-55.75, 3.5) * mm, "end": v(-55.75, 17.5) * mm});
            skLineSegment(sketch, "E67.right", {"start": v(-58.75, 3.5) * mm, "end": v(-58.75, 17.5) * mm});
            skPoint(sketch, "E67.middle", {"position": v(-57.25, 10.5) * mm});
            skSolve(sketch);
        }
        {
            var Q0;
            Q0=makeQuery(id+"F139.imprint","IMPRINT",FACE,{"disambiguationData":[TD([[makeQuery(id+"F139.imprint","IMPRINT",EDGE,{"derivedFrom":sQuery(id+"F139.wireOp",EDGE,"E67.bottom")}),-1.0]])]});
            extrude(context, id + "F140", {"entities" : qUnion([Q0]), "operationType" : NewBodyOperationType.ADD, "depth" : .5 * mm, "offsetDistance" : 25 * mm});
        }
        {
            var Q0;
            Q0=makeQuery(id+"F140.opExtrude","CAP_EDGE",EDGE,{"disambiguationData":[OSD([sQuery(id+"F139.wireOp",EDGE,"E67.top")])],"isStart":false});
            var Q1;
            Q1=makeQuery(id+"F140.opExtrude","CAP_EDGE",EDGE,{"disambiguationData":[OSD([sQuery(id+"F139.wireOp",EDGE,"E67.bottom")])],"isStart":false});
            chamfer(context, id + "F141", {"entities" : qUnion([Q0, Q1]), "chamferType" : ChamferType.TWO_OFFSETS, "width1" : 7 * mm, "oppositeDirection" : false, "width2" : .5 * mm, "tangentPropagation" : true});
        }
        {
            var Q0;
            Q0=makeQuery(id+"F1.opExtrude","SWEPT_FACE",FACE,{"disambiguationData":[OSD([sQuery(id+"F0.wireOp",EDGE,"E3.0")])]});
            var sketch = newSketch(context, id + "F142", { "sketchPlane" : qUnion([Q0])});
            skLineSegment(sketch, "E68.bottom", {"start": v(-22.84, 3.5) * mm, "end": v(-25.84, 3.5) * mm});
            skLineSegment(sketch, "E68.top", {"start": v(-22.84, 17.5) * mm, "end": v(-25.84, 17.5) * mm});
            skLineSegment(sketch, "E68.left", {"start": v(-22.84, 3.5) * mm, "end": v(-22.84, 17.5) * mm});
            skLineSegment(sketch, "E68.right", {"start": v(-25.84, 3.5) * mm, "end": v(-25.84, 17.5) * mm});
            skPoint(sketch, "E68.middle", {"position": v(-24.34, 10.5) * mm});
            skLineSegment(sketch, "E69.bottom", {"start": v(-88.66, 3.5) * mm, "end": v(-91.66, 3.5) * mm});
            skLineSegment(sketch, "E69.top", {"start": v(-88.66, 17.5) * mm, "end": v(-91.66, 17.5) * mm});
            skLineSegment(sketch, "E69.left", {"start": v(-88.66, 3.5) * mm, "end": v(-88.66, 17.5) * mm});
            skLineSegment(sketch, "E69.right", {"start": v(-91.66, 3.5) * mm, "end": v(-91.66, 17.5) * mm});
            skPoint(sketch, "E69.middle", {"position": v(-90.16, 10.5) * mm});
            skSolve(sketch);
        }
        {
            var Q0;
            Q0=makeQuery(id+"F142.imprint","IMPRINT",FACE,{"disambiguationData":[TD([[makeQuery(id+"F142.imprint","IMPRINT",EDGE,{"derivedFrom":sQuery(id+"F142.wireOp",EDGE,"E69.bottom")}),-1.0]])]});
            var Q1;
            Q1=makeQuery(id+"F142.imprint","IMPRINT",FACE,{"disambiguationData":[TD([[makeQuery(id+"F142.imprint","IMPRINT",EDGE,{"derivedFrom":sQuery(id+"F142.wireOp",EDGE,"E68.bottom")}),-1.0]])]});
            extrude(context, id + "F143", {"entities" : qUnion([Q0, Q1]), "operationType" : NewBodyOperationType.ADD, "depth" : .5 * mm, "offsetDistance" : 25 * mm});
        }
        {
            var Q0;
            Q0=makeQuery(id+"F143.opExtrude","CAP_EDGE",EDGE,{"disambiguationData":[OSD([sQuery(id+"F142.wireOp",EDGE,"E69.top")])],"isStart":false});
            var Q1;
            Q1=makeQuery(id+"F143.opExtrude","CAP_EDGE",EDGE,{"disambiguationData":[OSD([sQuery(id+"F142.wireOp",EDGE,"E69.bottom")])],"isStart":false});
            var Q2;
            Q2=makeQuery(id+"F143.opExtrude","CAP_EDGE",EDGE,{"disambiguationData":[OSD([sQuery(id+"F142.wireOp",EDGE,"E68.top")])],"isStart":false});
            chamfer(context, id + "F144", {"entities" : qUnion([Q0, Q1, Q2]), "chamferType" : ChamferType.TWO_OFFSETS, "width1" : 7 * mm, "oppositeDirection" : false, "width2" : .5 * mm, "tangentPropagation" : true});
        }
        {
            var Q0;
            Q0=makeQuery(id+"F143.opExtrude","CAP_EDGE",EDGE,{"disambiguationData":[OSD([sQuery(id+"F142.wireOp",EDGE,"E68.bottom")])],"isStart":false});
            chamfer(context, id + "F145", {"entities" : qUnion([Q0]), "chamferType" : ChamferType.TWO_OFFSETS, "width1" : 7 * mm, "oppositeDirection" : true, "width2" : .5 * mm, "tangentPropagation" : true});
        }
        {
            var Q0;
            Q0=makeQuery(id+"F1.opExtrude","SWEPT_FACE",FACE,{"disambiguationData":[OSD([sQuery(id+"F0.wireOp",EDGE,"E4.0")])]});
            var sketch = newSketch(context, id + "F146", { "sketchPlane" : qUnion([Q0])});
            skLineSegment(sketch, "E70.bottom", {"start": v(-55.75, 3.5) * mm, "end": v(-58.75, 3.5) * mm});
            skLineSegment(sketch, "E70.top", {"start": v(-55.75, 17.5) * mm, "end": v(-58.75, 17.5) * mm});
            skLineSegment(sketch, "E70.left", {"start": v(-55.75, 3.5) * mm, "end": v(-55.75, 17.5) * mm});
            skLineSegment(sketch, "E70.right", {"start": v(-58.75, 3.5) * mm, "end": v(-58.75, 17.5) * mm});
            skPoint(sketch, "E70.middle", {"position": v(-57.25, 10.5) * mm});
            skSolve(sketch);
        }
        {
            var Q0;
            Q0=makeQuery(id+"F146.imprint","IMPRINT",FACE,{"disambiguationData":[TD([[makeQuery(id+"F146.imprint","IMPRINT",EDGE,{"derivedFrom":sQuery(id+"F146.wireOp",EDGE,"E70.bottom")}),-1.0]])]});
            extrude(context, id + "F147", {"entities" : qUnion([Q0]), "operationType" : NewBodyOperationType.ADD, "depth" : .5 * mm, "offsetDistance" : 25 * mm});
        }
        {
            var Q0;
            Q0=makeQuery(id+"F147.opExtrude","CAP_EDGE",EDGE,{"disambiguationData":[OSD([sQuery(id+"F146.wireOp",EDGE,"E70.top")])],"isStart":false});
            var Q1;
            Q1=makeQuery(id+"F147.opExtrude","CAP_EDGE",EDGE,{"disambiguationData":[OSD([sQuery(id+"F146.wireOp",EDGE,"E70.bottom")])],"isStart":false});
            chamfer(context, id + "F148", {"entities" : qUnion([Q0, Q1]), "chamferType" : ChamferType.TWO_OFFSETS, "width1" : 7 * mm, "oppositeDirection" : false, "width2" : .5 * mm, "tangentPropagation" : true});
        }
        {
            var Q0;
            Q0=makeQuery(id+"F1.opExtrude","SWEPT_FACE",FACE,{"disambiguationData":[OSD([sQuery(id+"F0.wireOp",EDGE,"E5.0")])]});
            var sketch = newSketch(context, id + "F149", { "sketchPlane" : qUnion([Q0])});
            skLineSegment(sketch, "E71.bottom", {"start": v(-22.84, 3.5) * mm, "end": v(-25.84, 3.5) * mm});
            skLineSegment(sketch, "E71.top", {"start": v(-22.84, 17.5) * mm, "end": v(-25.84, 17.5) * mm});
            skLineSegment(sketch, "E71.left", {"start": v(-22.84, 3.5) * mm, "end": v(-22.84, 17.5) * mm});
            skLineSegment(sketch, "E71.right", {"start": v(-25.84, 3.5) * mm, "end": v(-25.84, 17.5) * mm});
            skPoint(sketch, "E71.middle", {"position": v(-24.34, 10.5) * mm});
            skLineSegment(sketch, "E72.bottom", {"start": v(-88.66, 3.5) * mm, "end": v(-91.66, 3.5) * mm});
            skLineSegment(sketch, "E72.top", {"start": v(-88.66, 17.5) * mm, "end": v(-91.66, 17.5) * mm});
            skLineSegment(sketch, "E72.left", {"start": v(-88.66, 3.5) * mm, "end": v(-88.66, 17.5) * mm});
            skLineSegment(sketch, "E72.right", {"start": v(-91.66, 3.5) * mm, "end": v(-91.66, 17.5) * mm});
            skPoint(sketch, "E72.middle", {"position": v(-90.16, 10.5) * mm});
            skSolve(sketch);
        }
        {
            var Q0;
            Q0=makeQuery(id+"F149.imprint","IMPRINT",FACE,{"disambiguationData":[TD([[makeQuery(id+"F149.imprint","IMPRINT",EDGE,{"derivedFrom":sQuery(id+"F149.wireOp",EDGE,"E72.bottom")}),-1.0]])]});
            var Q1;
            Q1=makeQuery(id+"F149.imprint","IMPRINT",FACE,{"disambiguationData":[TD([[makeQuery(id+"F149.imprint","IMPRINT",EDGE,{"derivedFrom":sQuery(id+"F149.wireOp",EDGE,"E71.bottom")}),-1.0]])]});
            extrude(context, id + "F150", {"entities" : qUnion([Q0, Q1]), "operationType" : NewBodyOperationType.ADD, "depth" : .5 * mm, "offsetDistance" : 25 * mm});
        }
        {
            var Q0;
            Q0=makeQuery(id+"F150.opExtrude","CAP_EDGE",EDGE,{"disambiguationData":[OSD([sQuery(id+"F149.wireOp",EDGE,"E72.top")])],"isStart":false});
            var Q1;
            Q1=makeQuery(id+"F150.opExtrude","CAP_EDGE",EDGE,{"disambiguationData":[OSD([sQuery(id+"F149.wireOp",EDGE,"E72.bottom")])],"isStart":false});
            var Q2;
            Q2=makeQuery(id+"F150.opExtrude","CAP_EDGE",EDGE,{"disambiguationData":[OSD([sQuery(id+"F149.wireOp",EDGE,"E71.top")])],"isStart":false});
            chamfer(context, id + "F151", {"entities" : qUnion([Q0, Q1, Q2]), "chamferType" : ChamferType.TWO_OFFSETS, "width1" : 7 * mm, "oppositeDirection" : false, "width2" : .5 * mm, "tangentPropagation" : true});
        }
        {
            var Q0;
            Q0=makeQuery(id+"F150.opExtrude","CAP_EDGE",EDGE,{"disambiguationData":[OSD([sQuery(id+"F149.wireOp",EDGE,"E71.bottom")])],"isStart":false});
            chamfer(context, id + "F152", {"entities" : qUnion([Q0]), "chamferType" : ChamferType.TWO_OFFSETS, "width1" : 7 * mm, "oppositeDirection" : true, "width2" : .5 * mm, "tangentPropagation" : true});
        }
        {
            var Q0;
            Q0=makeQuery(id+"F1.opExtrude","SWEPT_FACE",FACE,{"disambiguationData":[OSD([sQuery(id+"F0.wireOp",EDGE,"E7.0")])]});
            var sketch = newSketch(context, id + "F153", { "sketchPlane" : qUnion([Q0])});
            skLineSegment(sketch, "E73.bottom", {"start": v(-55.75, 3.5) * mm, "end": v(-58.75, 3.5) * mm});
            skLineSegment(sketch, "E73.top", {"start": v(-55.75, 17.5) * mm, "end": v(-58.75, 17.5) * mm});
            skLineSegment(sketch, "E73.left", {"start": v(-55.75, 3.5) * mm, "end": v(-55.75, 17.5) * mm});
            skLineSegment(sketch, "E73.right", {"start": v(-58.75, 3.5) * mm, "end": v(-58.75, 17.5) * mm});
            skPoint(sketch, "E73.middle", {"position": v(-57.25, 10.5) * mm});
            skSolve(sketch);
        }
        {
            var Q0;
            Q0=makeQuery(id+"F153.imprint","IMPRINT",FACE,{"disambiguationData":[TD([[makeQuery(id+"F153.imprint","IMPRINT",EDGE,{"derivedFrom":sQuery(id+"F153.wireOp",EDGE,"E73.bottom")}),-1.0]])]});
            extrude(context, id + "F154", {"entities" : qUnion([Q0]), "operationType" : NewBodyOperationType.ADD, "depth" : .5 * mm, "offsetDistance" : 25 * mm});
        }
        {
            var Q0;
            Q0=makeQuery(id+"F154.opExtrude","CAP_EDGE",EDGE,{"disambiguationData":[OSD([sQuery(id+"F153.wireOp",EDGE,"E73.top")])],"isStart":false});
            var Q1;
            Q1=makeQuery(id+"F154.opExtrude","CAP_EDGE",EDGE,{"disambiguationData":[OSD([sQuery(id+"F153.wireOp",EDGE,"E73.bottom")])],"isStart":false});
            chamfer(context, id + "F155", {"entities" : qUnion([Q0, Q1]), "chamferType" : ChamferType.TWO_OFFSETS, "width1" : 7 * mm, "oppositeDirection" : false, "width2" : .5 * mm, "tangentPropagation" : true});
        }
    });
